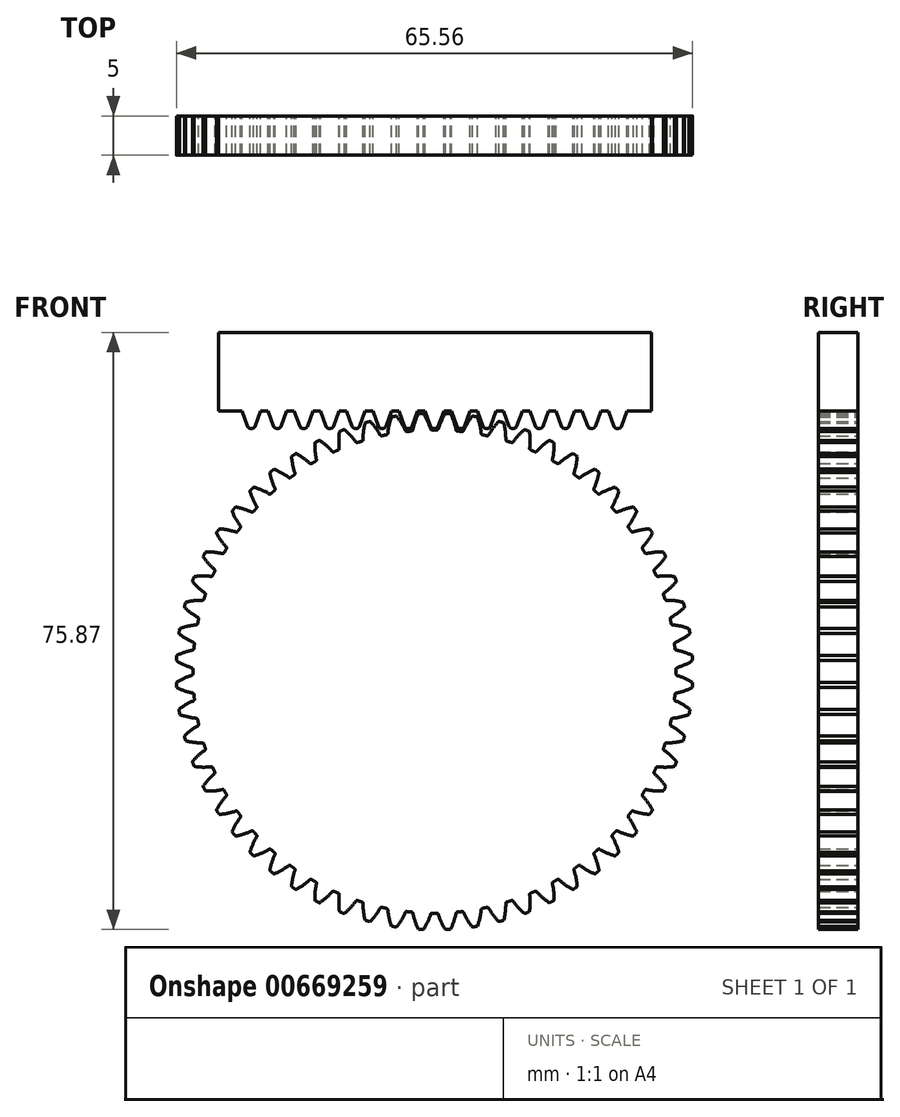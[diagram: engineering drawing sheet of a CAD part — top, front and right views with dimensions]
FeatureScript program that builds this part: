
annotation { "Feature Type Name" : "Feature", "Feature Type Description" : "" }
export const myFeature = defineFeature(function(context is Context, id is Id, definition is map)
    precondition{}
    {
        {
            var Q0;
            Q0=qCreatedBy(makeId("Front.planeOp"),FACE);
            var sketch = newSketch(context, id + "F0", { "sketchPlane" : qUnion([Q0])});
            skCircle(sketch, "E0", {"center": v(0, 0) * mm, "radius": 31.75 * mm, "construction": true});
            skCircle(sketch, "E1", {"center": v(0, 0) * mm, "radius": 30.7 * mm, "construction": true});
            skCircle(sketch, "E2", {"center": v(0, 0) * mm, "radius": 32.81 * mm, "construction": true});
            skCircle(sketch, "E3", {"center": v(0, 0) * mm, "radius": 29.63 * mm, "construction": true});
            skLineSegment(sketch, "E4", {"start": v(0, 0) * mm, "end": v(-1.03, 39.18) * mm, "construction": true});
            skLineSegment(sketch, "E5", {"start": v(0, 0) * mm, "end": v(-3.06, 38.83) * mm, "construction": true});
            skLineSegment(sketch, "E6", {"start": v(0, 0) * mm, "end": v(-2.1, 39.97) * mm, "construction": true});
            skLineSegment(sketch, "E7", {"start": v(-0.83, 31.74) * mm, "end": v(-20.7, 31.22) * mm, "construction": true});
            skLineSegment(sketch, "E8", {"start": v(-0.83, 31.74) * mm, "end": v(-21.46, 23.61) * mm, "construction": true});
            skCircle(sketch, "E9", {"center": v(-0.83, 31.74) * mm, "radius": 7.94 * mm, "construction": true});
            skArc(sketch, "E10", {"start": v(-0.5, 30.83) * mm, "mid": v(-0.88, 31.84) * mm, "end": v(-1.4, 32.78) * mm});
            skArc(sketch, "E11", {"start": v(-1.4, 32.78) * mm, "mid": v(-1.55, 32.77) * mm, "end": v(-1.72, 32.77) * mm});
            skArc(sketch, "E12", {"start": v(0, 30.7) * mm, "mid": v(-0.15, 30.69) * mm, "end": v(-0.3, 30.69) * mm});
            skArc(sketch, "E13.MirrorCS", {"start": v(-2.04, 32.75) * mm, "mid": v(-1.88, 32.76) * mm, "end": v(-1.72, 32.77) * mm});
            skArc(sketch, "E14.MirrorCS", {"start": v(-2.73, 30.71) * mm, "mid": v(-2.46, 31.75) * mm, "end": v(-2.04, 32.75) * mm});
            skArc(sketch, "E15.MirrorCS", {"start": v(-3.2, 30.52) * mm, "mid": v(-3.06, 30.54) * mm, "end": v(-2.91, 30.55) * mm});
            skPoint(sketch, "E16.visualSharp", {"position": v(-2.76, 30.57) * mm});
            skArc(sketch, "E16.filletArc", {"start": v(-2.91, 30.55) * mm, "mid": v(-2.8, 30.6) * mm, "end": v(-2.73, 30.71) * mm});
            skPoint(sketch, "E17.visualSharp", {"position": v(-0.45, 30.69) * mm});
            skArc(sketch, "E17.filletArc", {"start": v(-0.5, 30.83) * mm, "mid": v(-0.42, 30.73) * mm, "end": v(-0.3, 30.69) * mm});
            skArc(sketch, "E18.1.0", {"start": v(0, 30.7) * mm, "mid": v(0.15, 30.69) * mm, "end": v(0.3, 30.69) * mm});
            skArc(sketch, "E18.1.1", {"start": v(0.3, 30.69) * mm, "mid": v(0.42, 30.73) * mm, "end": v(0.5, 30.83) * mm});
            skArc(sketch, "E18.1.2", {"start": v(0.5, 30.83) * mm, "mid": v(0.88, 31.84) * mm, "end": v(1.4, 32.78) * mm});
            skArc(sketch, "E18.1.3", {"start": v(2.73, 30.71) * mm, "mid": v(2.8, 30.6) * mm, "end": v(2.91, 30.55) * mm});
            skArc(sketch, "E18.1.4", {"start": v(3.2, 30.52) * mm, "mid": v(3.06, 30.54) * mm, "end": v(2.91, 30.55) * mm});
            skArc(sketch, "E18.1.5", {"start": v(2.73, 30.71) * mm, "mid": v(2.46, 31.75) * mm, "end": v(2.04, 32.75) * mm});
            skArc(sketch, "E18.1.6", {"start": v(1.4, 32.78) * mm, "mid": v(1.55, 32.77) * mm, "end": v(1.72, 32.77) * mm});
            skArc(sketch, "E18.1.7", {"start": v(2.04, 32.75) * mm, "mid": v(1.88, 32.76) * mm, "end": v(1.72, 32.77) * mm});
            skArc(sketch, "E18.2.0", {"start": v(3.2, 30.52) * mm, "mid": v(3.36, 30.5) * mm, "end": v(3.5, 30.49) * mm});
            skArc(sketch, "E18.2.1", {"start": v(3.5, 30.49) * mm, "mid": v(3.63, 30.52) * mm, "end": v(3.71, 30.6) * mm});
            skArc(sketch, "E18.2.2", {"start": v(3.71, 30.6) * mm, "mid": v(4.2, 31.57) * mm, "end": v(4.81, 32.46) * mm});
            skArc(sketch, "E18.2.3", {"start": v(5.93, 30.26) * mm, "mid": v(5.98, 30.14) * mm, "end": v(6.09, 30.08) * mm});
            skArc(sketch, "E18.2.4", {"start": v(6.38, 30.02) * mm, "mid": v(6.24, 30.05) * mm, "end": v(6.09, 30.08) * mm});
            skArc(sketch, "E18.2.5", {"start": v(5.93, 30.26) * mm, "mid": v(5.76, 31.32) * mm, "end": v(5.45, 32.35) * mm});
            skArc(sketch, "E18.2.6", {"start": v(4.81, 32.46) * mm, "mid": v(4.97, 32.43) * mm, "end": v(5.13, 32.4) * mm});
            skArc(sketch, "E18.2.7", {"start": v(5.45, 32.35) * mm, "mid": v(5.3, 32.38) * mm, "end": v(5.13, 32.4) * mm});
            skArc(sketch, "E18.3.0", {"start": v(6.38, 30.02) * mm, "mid": v(6.53, 29.99) * mm, "end": v(6.67, 29.96) * mm});
            skArc(sketch, "E18.3.1", {"start": v(6.67, 29.96) * mm, "mid": v(6.8, 29.97) * mm, "end": v(6.89, 30.05) * mm});
            skArc(sketch, "E18.3.2", {"start": v(6.89, 30.05) * mm, "mid": v(7.47, 30.96) * mm, "end": v(8.18, 31.77) * mm});
            skArc(sketch, "E18.3.3", {"start": v(9.06, 29.47) * mm, "mid": v(9.1, 29.35) * mm, "end": v(9.2, 29.28) * mm});
            skArc(sketch, "E18.3.4", {"start": v(9.48, 29.19) * mm, "mid": v(9.34, 29.23) * mm, "end": v(9.2, 29.28) * mm});
            skArc(sketch, "E18.3.5", {"start": v(9.06, 29.47) * mm, "mid": v(9, 30.55) * mm, "end": v(8.8, 31.6) * mm});
            skArc(sketch, "E18.3.6", {"start": v(8.18, 31.77) * mm, "mid": v(8.33, 31.73) * mm, "end": v(8.5, 31.7) * mm});
            skArc(sketch, "E18.3.7", {"start": v(8.8, 31.6) * mm, "mid": v(8.65, 31.65) * mm, "end": v(8.5, 31.7) * mm});
            skArc(sketch, "E18.4.0", {"start": v(9.48, 29.19) * mm, "mid": v(9.63, 29.14) * mm, "end": v(9.77, 29.1) * mm});
            skArc(sketch, "E18.4.1", {"start": v(9.77, 29.1) * mm, "mid": v(9.9, 29.1) * mm, "end": v(10, 29.17) * mm});
            skArc(sketch, "E18.4.2", {"start": v(10, 29.17) * mm, "mid": v(10.67, 30) * mm, "end": v(11.45, 30.75) * mm});
            skArc(sketch, "E18.4.3", {"start": v(12.1, 28.36) * mm, "mid": v(12.12, 28.24) * mm, "end": v(12.21, 28.16) * mm});
            skArc(sketch, "E18.4.4", {"start": v(12.48, 28.04) * mm, "mid": v(12.35, 28.1) * mm, "end": v(12.21, 28.16) * mm});
            skArc(sketch, "E18.4.5", {"start": v(12.1, 28.36) * mm, "mid": v(12.15, 29.44) * mm, "end": v(12.06, 30.51) * mm});
            skArc(sketch, "E18.4.6", {"start": v(11.45, 30.75) * mm, "mid": v(11.6, 30.69) * mm, "end": v(11.76, 30.63) * mm});
            skArc(sketch, "E18.4.7", {"start": v(12.06, 30.51) * mm, "mid": v(11.9, 30.57) * mm, "end": v(11.76, 30.63) * mm});
            skArc(sketch, "E18.5.0", {"start": v(12.48, 28.04) * mm, "mid": v(12.62, 27.98) * mm, "end": v(12.75, 27.91) * mm});
            skArc(sketch, "E18.5.1", {"start": v(12.75, 27.91) * mm, "mid": v(12.88, 27.9) * mm, "end": v(12.99, 27.97) * mm});
            skArc(sketch, "E18.5.2", {"start": v(12.99, 27.97) * mm, "mid": v(13.75, 28.73) * mm, "end": v(14.6, 29.38) * mm});
            skArc(sketch, "E18.5.3", {"start": v(15, 26.94) * mm, "mid": v(15, 26.82) * mm, "end": v(15.09, 26.73) * mm});
            skArc(sketch, "E18.5.4", {"start": v(15.35, 26.58) * mm, "mid": v(15.22, 26.65) * mm, "end": v(15.09, 26.73) * mm});
            skArc(sketch, "E18.5.5", {"start": v(15, 26.94) * mm, "mid": v(15.16, 28) * mm, "end": v(15.18, 29.08) * mm});
            skArc(sketch, "E18.5.6", {"start": v(14.6, 29.38) * mm, "mid": v(14.75, 29.3) * mm, "end": v(14.9, 29.23) * mm});
            skArc(sketch, "E18.5.7", {"start": v(15.18, 29.08) * mm, "mid": v(15.04, 29.16) * mm, "end": v(14.9, 29.23) * mm});
            skArc(sketch, "E18.6.0", {"start": v(15.34, 26.58) * mm, "mid": v(15.47, 26.5) * mm, "end": v(15.6, 26.43) * mm});
            skArc(sketch, "E18.6.1", {"start": v(15.6, 26.43) * mm, "mid": v(15.73, 26.4) * mm, "end": v(15.84, 26.45) * mm});
            skArc(sketch, "E18.6.2", {"start": v(15.84, 26.45) * mm, "mid": v(16.68, 27.13) * mm, "end": v(17.6, 27.7) * mm});
            skArc(sketch, "E18.6.3", {"start": v(17.72, 25.23) * mm, "mid": v(17.72, 25.1) * mm, "end": v(17.8, 25) * mm});
            skArc(sketch, "E18.6.4", {"start": v(18.04, 24.83) * mm, "mid": v(17.92, 24.92) * mm, "end": v(17.8, 25) * mm});
            skArc(sketch, "E18.6.5", {"start": v(17.72, 25.23) * mm, "mid": v(18, 26.27) * mm, "end": v(18.14, 27.34) * mm});
            skArc(sketch, "E18.6.6", {"start": v(17.6, 27.7) * mm, "mid": v(17.73, 27.6) * mm, "end": v(17.87, 27.52) * mm});
            skArc(sketch, "E18.6.7", {"start": v(18.14, 27.34) * mm, "mid": v(18, 27.43) * mm, "end": v(17.87, 27.52) * mm});
            skArc(sketch, "E18.7.0", {"start": v(18.04, 24.83) * mm, "mid": v(18.16, 24.74) * mm, "end": v(18.28, 24.65) * mm});
            skArc(sketch, "E18.7.1", {"start": v(18.28, 24.65) * mm, "mid": v(18.4, 24.61) * mm, "end": v(18.52, 24.65) * mm});
            skArc(sketch, "E18.7.2", {"start": v(18.52, 24.65) * mm, "mid": v(19.42, 25.24) * mm, "end": v(20.4, 25.7) * mm});
            skArc(sketch, "E18.7.3", {"start": v(20.26, 23.24) * mm, "mid": v(20.25, 23.11) * mm, "end": v(20.31, 23) * mm});
            skArc(sketch, "E18.7.4", {"start": v(20.54, 22.8) * mm, "mid": v(20.42, 22.9) * mm, "end": v(20.31, 23) * mm});
            skArc(sketch, "E18.7.5", {"start": v(20.26, 23.24) * mm, "mid": v(20.65, 24.24) * mm, "end": v(20.9, 25.3) * mm});
            skArc(sketch, "E18.7.6", {"start": v(20.4, 25.7) * mm, "mid": v(20.52, 25.6) * mm, "end": v(20.65, 25.5) * mm});
            skArc(sketch, "E18.7.7", {"start": v(20.9, 25.3) * mm, "mid": v(20.77, 25.4) * mm, "end": v(20.65, 25.5) * mm});
            skArc(sketch, "E18.8.0", {"start": v(20.54, 22.8) * mm, "mid": v(20.65, 22.7) * mm, "end": v(20.76, 22.6) * mm});
            skArc(sketch, "E18.8.1", {"start": v(20.76, 22.6) * mm, "mid": v(20.87, 22.56) * mm, "end": v(21, 22.58) * mm});
            skArc(sketch, "E18.8.2", {"start": v(21, 22.58) * mm, "mid": v(21.95, 23.07) * mm, "end": v(22.97, 23.43) * mm});
            skArc(sketch, "E18.8.3", {"start": v(22.58, 21) * mm, "mid": v(22.56, 20.87) * mm, "end": v(22.6, 20.76) * mm});
            skArc(sketch, "E18.8.4", {"start": v(22.8, 20.54) * mm, "mid": v(22.7, 20.65) * mm, "end": v(22.6, 20.76) * mm});
            skArc(sketch, "E18.8.5", {"start": v(22.58, 21) * mm, "mid": v(23.07, 21.95) * mm, "end": v(23.43, 22.97) * mm});
            skArc(sketch, "E18.8.6", {"start": v(22.97, 23.43) * mm, "mid": v(23.08, 23.31) * mm, "end": v(23.2, 23.2) * mm});
            skArc(sketch, "E18.8.7", {"start": v(23.43, 22.97) * mm, "mid": v(23.31, 23.08) * mm, "end": v(23.2, 23.2) * mm});
            skArc(sketch, "E18.9.0", {"start": v(22.8, 20.54) * mm, "mid": v(22.9, 20.42) * mm, "end": v(23, 20.31) * mm});
            skArc(sketch, "E18.9.1", {"start": v(23, 20.31) * mm, "mid": v(23.11, 20.25) * mm, "end": v(23.24, 20.26) * mm});
            skArc(sketch, "E18.9.2", {"start": v(23.24, 20.26) * mm, "mid": v(24.24, 20.65) * mm, "end": v(25.3, 20.9) * mm});
            skArc(sketch, "E18.9.3", {"start": v(24.65, 18.52) * mm, "mid": v(24.61, 18.4) * mm, "end": v(24.65, 18.28) * mm});
            skArc(sketch, "E18.9.4", {"start": v(24.83, 18.04) * mm, "mid": v(24.74, 18.16) * mm, "end": v(24.65, 18.28) * mm});
            skArc(sketch, "E18.9.5", {"start": v(24.65, 18.52) * mm, "mid": v(25.24, 19.42) * mm, "end": v(25.7, 20.4) * mm});
            skArc(sketch, "E18.9.6", {"start": v(25.3, 20.9) * mm, "mid": v(25.4, 20.77) * mm, "end": v(25.5, 20.65) * mm});
            skArc(sketch, "E18.9.7", {"start": v(25.7, 20.4) * mm, "mid": v(25.6, 20.52) * mm, "end": v(25.5, 20.65) * mm});
            skArc(sketch, "E18.10.0", {"start": v(24.83, 18.04) * mm, "mid": v(24.92, 17.92) * mm, "end": v(25, 17.8) * mm});
            skArc(sketch, "E18.10.1", {"start": v(25, 17.8) * mm, "mid": v(25.1, 17.72) * mm, "end": v(25.23, 17.72) * mm});
            skArc(sketch, "E18.10.2", {"start": v(25.23, 17.72) * mm, "mid": v(26.27, 18) * mm, "end": v(27.34, 18.14) * mm});
            skArc(sketch, "E18.10.3", {"start": v(26.45, 15.84) * mm, "mid": v(26.4, 15.73) * mm, "end": v(26.43, 15.6) * mm});
            skArc(sketch, "E18.10.4", {"start": v(26.58, 15.35) * mm, "mid": v(26.5, 15.47) * mm, "end": v(26.43, 15.6) * mm});
            skArc(sketch, "E18.10.5", {"start": v(26.45, 15.84) * mm, "mid": v(27.13, 16.68) * mm, "end": v(27.7, 17.6) * mm});
            skArc(sketch, "E18.10.6", {"start": v(27.34, 18.14) * mm, "mid": v(27.43, 18) * mm, "end": v(27.52, 17.87) * mm});
            skArc(sketch, "E18.10.7", {"start": v(27.7, 17.6) * mm, "mid": v(27.6, 17.73) * mm, "end": v(27.52, 17.87) * mm});
            skArc(sketch, "E18.11.0", {"start": v(26.58, 15.35) * mm, "mid": v(26.65, 15.22) * mm, "end": v(26.73, 15.09) * mm});
            skArc(sketch, "E18.11.1", {"start": v(26.73, 15.09) * mm, "mid": v(26.82, 15) * mm, "end": v(26.94, 15) * mm});
            skArc(sketch, "E18.11.2", {"start": v(26.94, 15) * mm, "mid": v(28, 15.16) * mm, "end": v(29.08, 15.18) * mm});
            skArc(sketch, "E18.11.3", {"start": v(27.97, 12.99) * mm, "mid": v(27.9, 12.88) * mm, "end": v(27.91, 12.75) * mm});
            skArc(sketch, "E18.11.4", {"start": v(28.04, 12.48) * mm, "mid": v(27.98, 12.62) * mm, "end": v(27.91, 12.75) * mm});
            skArc(sketch, "E18.11.5", {"start": v(27.97, 12.99) * mm, "mid": v(28.73, 13.75) * mm, "end": v(29.38, 14.6) * mm});
            skArc(sketch, "E18.11.6", {"start": v(29.08, 15.18) * mm, "mid": v(29.16, 15.04) * mm, "end": v(29.23, 14.9) * mm});
            skArc(sketch, "E18.11.7", {"start": v(29.38, 14.6) * mm, "mid": v(29.3, 14.75) * mm, "end": v(29.23, 14.9) * mm});
            skArc(sketch, "E18.12.0", {"start": v(28.04, 12.48) * mm, "mid": v(28.1, 12.35) * mm, "end": v(28.16, 12.21) * mm});
            skArc(sketch, "E18.12.1", {"start": v(28.16, 12.21) * mm, "mid": v(28.24, 12.12) * mm, "end": v(28.36, 12.1) * mm});
            skArc(sketch, "E18.12.2", {"start": v(28.36, 12.1) * mm, "mid": v(29.44, 12.15) * mm, "end": v(30.51, 12.06) * mm});
            skArc(sketch, "E18.12.3", {"start": v(29.17, 10) * mm, "mid": v(29.1, 9.9) * mm, "end": v(29.1, 9.77) * mm});
            skArc(sketch, "E18.12.4", {"start": v(29.19, 9.48) * mm, "mid": v(29.14, 9.63) * mm, "end": v(29.1, 9.77) * mm});
            skArc(sketch, "E18.12.5", {"start": v(29.17, 10) * mm, "mid": v(30, 10.67) * mm, "end": v(30.75, 11.45) * mm});
            skArc(sketch, "E18.12.6", {"start": v(30.51, 12.06) * mm, "mid": v(30.57, 11.9) * mm, "end": v(30.63, 11.76) * mm});
            skArc(sketch, "E18.12.7", {"start": v(30.75, 11.45) * mm, "mid": v(30.69, 11.6) * mm, "end": v(30.63, 11.76) * mm});
            skArc(sketch, "E18.13.0", {"start": v(29.19, 9.48) * mm, "mid": v(29.23, 9.34) * mm, "end": v(29.28, 9.2) * mm});
            skArc(sketch, "E18.13.1", {"start": v(29.28, 9.2) * mm, "mid": v(29.35, 9.1) * mm, "end": v(29.47, 9.06) * mm});
            skArc(sketch, "E18.13.2", {"start": v(29.47, 9.06) * mm, "mid": v(30.55, 9) * mm, "end": v(31.6, 8.8) * mm});
            skArc(sketch, "E18.13.3", {"start": v(30.05, 6.89) * mm, "mid": v(29.97, 6.8) * mm, "end": v(29.96, 6.67) * mm});
            skArc(sketch, "E18.13.4", {"start": v(30.02, 6.38) * mm, "mid": v(29.99, 6.53) * mm, "end": v(29.96, 6.67) * mm});
            skArc(sketch, "E18.13.5", {"start": v(30.05, 6.89) * mm, "mid": v(30.96, 7.47) * mm, "end": v(31.77, 8.18) * mm});
            skArc(sketch, "E18.13.6", {"start": v(31.6, 8.8) * mm, "mid": v(31.65, 8.65) * mm, "end": v(31.7, 8.5) * mm});
            skArc(sketch, "E18.13.7", {"start": v(31.77, 8.18) * mm, "mid": v(31.73, 8.33) * mm, "end": v(31.7, 8.5) * mm});
            skArc(sketch, "E18.14.0", {"start": v(30.02, 6.38) * mm, "mid": v(30.05, 6.24) * mm, "end": v(30.08, 6.09) * mm});
            skArc(sketch, "E18.14.1", {"start": v(30.08, 6.09) * mm, "mid": v(30.14, 5.98) * mm, "end": v(30.26, 5.93) * mm});
            skArc(sketch, "E18.14.2", {"start": v(30.26, 5.93) * mm, "mid": v(31.32, 5.76) * mm, "end": v(32.35, 5.45) * mm});
            skArc(sketch, "E18.14.3", {"start": v(30.6, 3.71) * mm, "mid": v(30.52, 3.63) * mm, "end": v(30.49, 3.5) * mm});
            skArc(sketch, "E18.14.4", {"start": v(30.52, 3.2) * mm, "mid": v(30.5, 3.36) * mm, "end": v(30.49, 3.5) * mm});
            skArc(sketch, "E18.14.5", {"start": v(30.6, 3.71) * mm, "mid": v(31.57, 4.2) * mm, "end": v(32.46, 4.81) * mm});
            skArc(sketch, "E18.14.6", {"start": v(32.35, 5.45) * mm, "mid": v(32.38, 5.3) * mm, "end": v(32.4, 5.13) * mm});
            skArc(sketch, "E18.14.7", {"start": v(32.46, 4.81) * mm, "mid": v(32.43, 4.97) * mm, "end": v(32.4, 5.13) * mm});
            skArc(sketch, "E18.15.0", {"start": v(30.52, 3.2) * mm, "mid": v(30.54, 3.06) * mm, "end": v(30.55, 2.91) * mm});
            skArc(sketch, "E18.15.1", {"start": v(30.55, 2.91) * mm, "mid": v(30.6, 2.8) * mm, "end": v(30.71, 2.73) * mm});
            skArc(sketch, "E18.15.2", {"start": v(30.71, 2.73) * mm, "mid": v(31.75, 2.46) * mm, "end": v(32.75, 2.04) * mm});
            skArc(sketch, "E18.15.3", {"start": v(30.83, 0.5) * mm, "mid": v(30.73, 0.42) * mm, "end": v(30.69, 0.3) * mm});
            skArc(sketch, "E18.15.4", {"start": v(30.7, 0) * mm, "mid": v(30.69, 0.15) * mm, "end": v(30.69, 0.3) * mm});
            skArc(sketch, "E18.15.5", {"start": v(30.83, 0.5) * mm, "mid": v(31.84, 0.88) * mm, "end": v(32.78, 1.4) * mm});
            skArc(sketch, "E18.15.6", {"start": v(32.75, 2.04) * mm, "mid": v(32.76, 1.88) * mm, "end": v(32.77, 1.72) * mm});
            skArc(sketch, "E18.15.7", {"start": v(32.78, 1.4) * mm, "mid": v(32.77, 1.55) * mm, "end": v(32.77, 1.72) * mm});
            skArc(sketch, "E18.16.0", {"start": v(30.7, 0) * mm, "mid": v(30.69, -0.15) * mm, "end": v(30.69, -0.3) * mm});
            skArc(sketch, "E18.16.1", {"start": v(30.69, -0.3) * mm, "mid": v(30.73, -0.42) * mm, "end": v(30.83, -0.5) * mm});
            skArc(sketch, "E18.16.2", {"start": v(30.83, -0.5) * mm, "mid": v(31.84, -0.88) * mm, "end": v(32.78, -1.4) * mm});
            skArc(sketch, "E18.16.3", {"start": v(30.71, -2.73) * mm, "mid": v(30.6, -2.8) * mm, "end": v(30.55, -2.91) * mm});
            skArc(sketch, "E18.16.4", {"start": v(30.52, -3.2) * mm, "mid": v(30.54, -3.06) * mm, "end": v(30.55, -2.91) * mm});
            skArc(sketch, "E18.16.5", {"start": v(30.71, -2.73) * mm, "mid": v(31.75, -2.46) * mm, "end": v(32.75, -2.04) * mm});
            skArc(sketch, "E18.16.6", {"start": v(32.78, -1.4) * mm, "mid": v(32.77, -1.55) * mm, "end": v(32.77, -1.72) * mm});
            skArc(sketch, "E18.16.7", {"start": v(32.75, -2.04) * mm, "mid": v(32.76, -1.88) * mm, "end": v(32.77, -1.72) * mm});
            skArc(sketch, "E18.17.0", {"start": v(30.52, -3.2) * mm, "mid": v(30.5, -3.36) * mm, "end": v(30.49, -3.5) * mm});
            skArc(sketch, "E18.17.1", {"start": v(30.49, -3.5) * mm, "mid": v(30.52, -3.63) * mm, "end": v(30.6, -3.71) * mm});
            skArc(sketch, "E18.17.2", {"start": v(30.6, -3.71) * mm, "mid": v(31.57, -4.2) * mm, "end": v(32.46, -4.81) * mm});
            skArc(sketch, "E18.17.3", {"start": v(30.26, -5.93) * mm, "mid": v(30.14, -5.98) * mm, "end": v(30.08, -6.09) * mm});
            skArc(sketch, "E18.17.4", {"start": v(30.02, -6.38) * mm, "mid": v(30.05, -6.24) * mm, "end": v(30.08, -6.09) * mm});
            skArc(sketch, "E18.17.5", {"start": v(30.26, -5.93) * mm, "mid": v(31.32, -5.76) * mm, "end": v(32.35, -5.45) * mm});
            skArc(sketch, "E18.17.6", {"start": v(32.46, -4.81) * mm, "mid": v(32.43, -4.97) * mm, "end": v(32.4, -5.13) * mm});
            skArc(sketch, "E18.17.7", {"start": v(32.35, -5.45) * mm, "mid": v(32.38, -5.3) * mm, "end": v(32.4, -5.13) * mm});
            skArc(sketch, "E18.18.0", {"start": v(30.02, -6.38) * mm, "mid": v(29.99, -6.53) * mm, "end": v(29.96, -6.67) * mm});
            skArc(sketch, "E18.18.1", {"start": v(29.96, -6.67) * mm, "mid": v(29.97, -6.8) * mm, "end": v(30.05, -6.89) * mm});
            skArc(sketch, "E18.18.2", {"start": v(30.05, -6.89) * mm, "mid": v(30.96, -7.47) * mm, "end": v(31.77, -8.18) * mm});
            skArc(sketch, "E18.18.3", {"start": v(29.47, -9.06) * mm, "mid": v(29.35, -9.1) * mm, "end": v(29.28, -9.2) * mm});
            skArc(sketch, "E18.18.4", {"start": v(29.19, -9.48) * mm, "mid": v(29.23, -9.34) * mm, "end": v(29.28, -9.2) * mm});
            skArc(sketch, "E18.18.5", {"start": v(29.47, -9.06) * mm, "mid": v(30.55, -9) * mm, "end": v(31.6, -8.8) * mm});
            skArc(sketch, "E18.18.6", {"start": v(31.77, -8.18) * mm, "mid": v(31.73, -8.33) * mm, "end": v(31.7, -8.5) * mm});
            skArc(sketch, "E18.18.7", {"start": v(31.6, -8.8) * mm, "mid": v(31.65, -8.65) * mm, "end": v(31.7, -8.5) * mm});
            skArc(sketch, "E18.19.0", {"start": v(29.19, -9.48) * mm, "mid": v(29.14, -9.63) * mm, "end": v(29.1, -9.77) * mm});
            skArc(sketch, "E18.19.1", {"start": v(29.1, -9.77) * mm, "mid": v(29.1, -9.9) * mm, "end": v(29.17, -10) * mm});
            skArc(sketch, "E18.19.2", {"start": v(29.17, -10) * mm, "mid": v(30, -10.67) * mm, "end": v(30.75, -11.45) * mm});
            skArc(sketch, "E18.19.3", {"start": v(28.36, -12.1) * mm, "mid": v(28.24, -12.12) * mm, "end": v(28.16, -12.21) * mm});
            skArc(sketch, "E18.19.4", {"start": v(28.04, -12.48) * mm, "mid": v(28.1, -12.35) * mm, "end": v(28.16, -12.21) * mm});
            skArc(sketch, "E18.19.5", {"start": v(28.36, -12.1) * mm, "mid": v(29.44, -12.15) * mm, "end": v(30.51, -12.06) * mm});
            skArc(sketch, "E18.19.6", {"start": v(30.75, -11.45) * mm, "mid": v(30.69, -11.6) * mm, "end": v(30.63, -11.76) * mm});
            skArc(sketch, "E18.19.7", {"start": v(30.51, -12.06) * mm, "mid": v(30.57, -11.9) * mm, "end": v(30.63, -11.76) * mm});
            skArc(sketch, "E18.20.0", {"start": v(28.04, -12.48) * mm, "mid": v(27.98, -12.62) * mm, "end": v(27.91, -12.75) * mm});
            skArc(sketch, "E18.20.1", {"start": v(27.91, -12.75) * mm, "mid": v(27.9, -12.88) * mm, "end": v(27.97, -12.99) * mm});
            skArc(sketch, "E18.20.2", {"start": v(27.97, -12.99) * mm, "mid": v(28.73, -13.75) * mm, "end": v(29.38, -14.6) * mm});
            skArc(sketch, "E18.20.3", {"start": v(26.94, -15) * mm, "mid": v(26.82, -15) * mm, "end": v(26.73, -15.09) * mm});
            skArc(sketch, "E18.20.4", {"start": v(26.58, -15.34) * mm, "mid": v(26.65, -15.22) * mm, "end": v(26.73, -15.09) * mm});
            skArc(sketch, "E18.20.5", {"start": v(26.94, -15) * mm, "mid": v(28, -15.16) * mm, "end": v(29.08, -15.18) * mm});
            skArc(sketch, "E18.20.6", {"start": v(29.38, -14.6) * mm, "mid": v(29.3, -14.75) * mm, "end": v(29.23, -14.9) * mm});
            skArc(sketch, "E18.20.7", {"start": v(29.08, -15.18) * mm, "mid": v(29.16, -15.04) * mm, "end": v(29.23, -14.9) * mm});
            skArc(sketch, "E18.21.0", {"start": v(26.58, -15.34) * mm, "mid": v(26.5, -15.47) * mm, "end": v(26.43, -15.6) * mm});
            skArc(sketch, "E18.21.1", {"start": v(26.43, -15.6) * mm, "mid": v(26.4, -15.73) * mm, "end": v(26.45, -15.84) * mm});
            skArc(sketch, "E18.21.2", {"start": v(26.45, -15.84) * mm, "mid": v(27.13, -16.68) * mm, "end": v(27.7, -17.6) * mm});
            skArc(sketch, "E18.21.3", {"start": v(25.23, -17.72) * mm, "mid": v(25.1, -17.72) * mm, "end": v(25, -17.8) * mm});
            skArc(sketch, "E18.21.4", {"start": v(24.83, -18.04) * mm, "mid": v(24.92, -17.92) * mm, "end": v(25, -17.8) * mm});
            skArc(sketch, "E18.21.5", {"start": v(25.23, -17.72) * mm, "mid": v(26.27, -18) * mm, "end": v(27.34, -18.14) * mm});
            skArc(sketch, "E18.21.6", {"start": v(27.7, -17.6) * mm, "mid": v(27.6, -17.73) * mm, "end": v(27.52, -17.87) * mm});
            skArc(sketch, "E18.21.7", {"start": v(27.34, -18.14) * mm, "mid": v(27.43, -18) * mm, "end": v(27.52, -17.87) * mm});
            skArc(sketch, "E18.22.0", {"start": v(24.83, -18.04) * mm, "mid": v(24.74, -18.16) * mm, "end": v(24.65, -18.28) * mm});
            skArc(sketch, "E18.22.1", {"start": v(24.65, -18.28) * mm, "mid": v(24.61, -18.4) * mm, "end": v(24.65, -18.52) * mm});
            skArc(sketch, "E18.22.2", {"start": v(24.65, -18.52) * mm, "mid": v(25.24, -19.42) * mm, "end": v(25.7, -20.4) * mm});
            skArc(sketch, "E18.22.3", {"start": v(23.24, -20.26) * mm, "mid": v(23.11, -20.25) * mm, "end": v(23, -20.31) * mm});
            skArc(sketch, "E18.22.4", {"start": v(22.8, -20.54) * mm, "mid": v(22.9, -20.42) * mm, "end": v(23, -20.31) * mm});
            skArc(sketch, "E18.22.5", {"start": v(23.24, -20.26) * mm, "mid": v(24.24, -20.65) * mm, "end": v(25.3, -20.9) * mm});
            skArc(sketch, "E18.22.6", {"start": v(25.7, -20.4) * mm, "mid": v(25.6, -20.52) * mm, "end": v(25.5, -20.65) * mm});
            skArc(sketch, "E18.22.7", {"start": v(25.3, -20.9) * mm, "mid": v(25.4, -20.77) * mm, "end": v(25.5, -20.65) * mm});
            skArc(sketch, "E18.23.0", {"start": v(22.8, -20.54) * mm, "mid": v(22.7, -20.65) * mm, "end": v(22.6, -20.76) * mm});
            skArc(sketch, "E18.23.1", {"start": v(22.6, -20.76) * mm, "mid": v(22.56, -20.87) * mm, "end": v(22.58, -21) * mm});
            skArc(sketch, "E18.23.2", {"start": v(22.58, -21) * mm, "mid": v(23.07, -21.95) * mm, "end": v(23.43, -22.97) * mm});
            skArc(sketch, "E18.23.3", {"start": v(21, -22.58) * mm, "mid": v(20.87, -22.56) * mm, "end": v(20.76, -22.6) * mm});
            skArc(sketch, "E18.23.4", {"start": v(20.54, -22.8) * mm, "mid": v(20.65, -22.7) * mm, "end": v(20.76, -22.6) * mm});
            skArc(sketch, "E18.23.5", {"start": v(21, -22.58) * mm, "mid": v(21.95, -23.07) * mm, "end": v(22.97, -23.43) * mm});
            skArc(sketch, "E18.23.6", {"start": v(23.43, -22.97) * mm, "mid": v(23.31, -23.08) * mm, "end": v(23.2, -23.2) * mm});
            skArc(sketch, "E18.23.7", {"start": v(22.97, -23.43) * mm, "mid": v(23.08, -23.31) * mm, "end": v(23.2, -23.2) * mm});
            skArc(sketch, "E18.24.0", {"start": v(20.54, -22.8) * mm, "mid": v(20.42, -22.9) * mm, "end": v(20.31, -23) * mm});
            skArc(sketch, "E18.24.1", {"start": v(20.31, -23) * mm, "mid": v(20.25, -23.11) * mm, "end": v(20.26, -23.24) * mm});
            skArc(sketch, "E18.24.2", {"start": v(20.26, -23.24) * mm, "mid": v(20.65, -24.24) * mm, "end": v(20.9, -25.3) * mm});
            skArc(sketch, "E18.24.3", {"start": v(18.52, -24.65) * mm, "mid": v(18.4, -24.61) * mm, "end": v(18.28, -24.65) * mm});
            skArc(sketch, "E18.24.4", {"start": v(18.04, -24.83) * mm, "mid": v(18.16, -24.74) * mm, "end": v(18.28, -24.65) * mm});
            skArc(sketch, "E18.24.5", {"start": v(18.52, -24.65) * mm, "mid": v(19.42, -25.24) * mm, "end": v(20.4, -25.7) * mm});
            skArc(sketch, "E18.24.6", {"start": v(20.9, -25.3) * mm, "mid": v(20.77, -25.4) * mm, "end": v(20.65, -25.5) * mm});
            skArc(sketch, "E18.24.7", {"start": v(20.4, -25.7) * mm, "mid": v(20.52, -25.6) * mm, "end": v(20.65, -25.5) * mm});
            skArc(sketch, "E18.25.0", {"start": v(18.04, -24.83) * mm, "mid": v(17.92, -24.92) * mm, "end": v(17.8, -25) * mm});
            skArc(sketch, "E18.25.1", {"start": v(17.8, -25) * mm, "mid": v(17.72, -25.1) * mm, "end": v(17.72, -25.23) * mm});
            skArc(sketch, "E18.25.2", {"start": v(17.72, -25.23) * mm, "mid": v(18, -26.27) * mm, "end": v(18.14, -27.34) * mm});
            skArc(sketch, "E18.25.3", {"start": v(15.84, -26.45) * mm, "mid": v(15.73, -26.4) * mm, "end": v(15.6, -26.43) * mm});
            skArc(sketch, "E18.25.4", {"start": v(15.35, -26.58) * mm, "mid": v(15.47, -26.5) * mm, "end": v(15.6, -26.43) * mm});
            skArc(sketch, "E18.25.5", {"start": v(15.84, -26.45) * mm, "mid": v(16.68, -27.13) * mm, "end": v(17.6, -27.7) * mm});
            skArc(sketch, "E18.25.6", {"start": v(18.14, -27.34) * mm, "mid": v(18, -27.43) * mm, "end": v(17.87, -27.52) * mm});
            skArc(sketch, "E18.25.7", {"start": v(17.6, -27.7) * mm, "mid": v(17.73, -27.6) * mm, "end": v(17.87, -27.52) * mm});
            skArc(sketch, "E18.26.0", {"start": v(15.35, -26.58) * mm, "mid": v(15.22, -26.65) * mm, "end": v(15.09, -26.73) * mm});
            skArc(sketch, "E18.26.1", {"start": v(15.09, -26.73) * mm, "mid": v(15, -26.82) * mm, "end": v(15, -26.94) * mm});
            skArc(sketch, "E18.26.2", {"start": v(15, -26.94) * mm, "mid": v(15.16, -28) * mm, "end": v(15.18, -29.08) * mm});
            skArc(sketch, "E18.26.3", {"start": v(12.99, -27.97) * mm, "mid": v(12.88, -27.9) * mm, "end": v(12.75, -27.91) * mm});
            skArc(sketch, "E18.26.4", {"start": v(12.48, -28.04) * mm, "mid": v(12.62, -27.98) * mm, "end": v(12.75, -27.91) * mm});
            skArc(sketch, "E18.26.5", {"start": v(12.99, -27.97) * mm, "mid": v(13.75, -28.73) * mm, "end": v(14.6, -29.38) * mm});
            skArc(sketch, "E18.26.6", {"start": v(15.18, -29.08) * mm, "mid": v(15.04, -29.16) * mm, "end": v(14.9, -29.23) * mm});
            skArc(sketch, "E18.26.7", {"start": v(14.6, -29.38) * mm, "mid": v(14.75, -29.3) * mm, "end": v(14.9, -29.23) * mm});
            skArc(sketch, "E18.27.0", {"start": v(12.48, -28.04) * mm, "mid": v(12.35, -28.1) * mm, "end": v(12.21, -28.16) * mm});
            skArc(sketch, "E18.27.1", {"start": v(12.21, -28.16) * mm, "mid": v(12.12, -28.24) * mm, "end": v(12.1, -28.36) * mm});
            skArc(sketch, "E18.27.2", {"start": v(12.1, -28.36) * mm, "mid": v(12.15, -29.44) * mm, "end": v(12.06, -30.51) * mm});
            skArc(sketch, "E18.27.3", {"start": v(10, -29.17) * mm, "mid": v(9.9, -29.1) * mm, "end": v(9.77, -29.1) * mm});
            skArc(sketch, "E18.27.4", {"start": v(9.48, -29.19) * mm, "mid": v(9.63, -29.14) * mm, "end": v(9.77, -29.1) * mm});
            skArc(sketch, "E18.27.5", {"start": v(10, -29.17) * mm, "mid": v(10.67, -30) * mm, "end": v(11.45, -30.75) * mm});
            skArc(sketch, "E18.27.6", {"start": v(12.06, -30.51) * mm, "mid": v(11.9, -30.57) * mm, "end": v(11.76, -30.63) * mm});
            skArc(sketch, "E18.27.7", {"start": v(11.45, -30.75) * mm, "mid": v(11.6, -30.69) * mm, "end": v(11.76, -30.63) * mm});
            skArc(sketch, "E18.28.0", {"start": v(9.48, -29.19) * mm, "mid": v(9.34, -29.23) * mm, "end": v(9.2, -29.28) * mm});
            skArc(sketch, "E18.28.1", {"start": v(9.2, -29.28) * mm, "mid": v(9.1, -29.35) * mm, "end": v(9.06, -29.47) * mm});
            skArc(sketch, "E18.28.2", {"start": v(9.06, -29.47) * mm, "mid": v(9, -30.55) * mm, "end": v(8.8, -31.6) * mm});
            skArc(sketch, "E18.28.3", {"start": v(6.89, -30.05) * mm, "mid": v(6.8, -29.97) * mm, "end": v(6.67, -29.96) * mm});
            skArc(sketch, "E18.28.4", {"start": v(6.38, -30.02) * mm, "mid": v(6.53, -29.99) * mm, "end": v(6.67, -29.96) * mm});
            skArc(sketch, "E18.28.5", {"start": v(6.89, -30.05) * mm, "mid": v(7.47, -30.96) * mm, "end": v(8.18, -31.77) * mm});
            skArc(sketch, "E18.28.6", {"start": v(8.8, -31.6) * mm, "mid": v(8.65, -31.65) * mm, "end": v(8.5, -31.7) * mm});
            skArc(sketch, "E18.28.7", {"start": v(8.18, -31.77) * mm, "mid": v(8.33, -31.73) * mm, "end": v(8.5, -31.7) * mm});
            skArc(sketch, "E18.29.0", {"start": v(6.38, -30.02) * mm, "mid": v(6.24, -30.05) * mm, "end": v(6.09, -30.08) * mm});
            skArc(sketch, "E18.29.1", {"start": v(6.09, -30.08) * mm, "mid": v(5.98, -30.14) * mm, "end": v(5.93, -30.26) * mm});
            skArc(sketch, "E18.29.2", {"start": v(5.93, -30.26) * mm, "mid": v(5.76, -31.32) * mm, "end": v(5.45, -32.35) * mm});
            skArc(sketch, "E18.29.3", {"start": v(3.71, -30.6) * mm, "mid": v(3.63, -30.52) * mm, "end": v(3.5, -30.49) * mm});
            skArc(sketch, "E18.29.4", {"start": v(3.2, -30.52) * mm, "mid": v(3.36, -30.5) * mm, "end": v(3.5, -30.49) * mm});
            skArc(sketch, "E18.29.5", {"start": v(3.71, -30.6) * mm, "mid": v(4.2, -31.57) * mm, "end": v(4.81, -32.46) * mm});
            skArc(sketch, "E18.29.6", {"start": v(5.45, -32.35) * mm, "mid": v(5.3, -32.38) * mm, "end": v(5.13, -32.4) * mm});
            skArc(sketch, "E18.29.7", {"start": v(4.81, -32.46) * mm, "mid": v(4.97, -32.43) * mm, "end": v(5.13, -32.4) * mm});
            skArc(sketch, "E18.30.0", {"start": v(3.2, -30.52) * mm, "mid": v(3.06, -30.54) * mm, "end": v(2.91, -30.55) * mm});
            skArc(sketch, "E18.30.1", {"start": v(2.91, -30.55) * mm, "mid": v(2.8, -30.6) * mm, "end": v(2.73, -30.71) * mm});
            skArc(sketch, "E18.30.2", {"start": v(2.73, -30.71) * mm, "mid": v(2.46, -31.75) * mm, "end": v(2.04, -32.75) * mm});
            skArc(sketch, "E18.30.3", {"start": v(0.5, -30.83) * mm, "mid": v(0.42, -30.73) * mm, "end": v(0.3, -30.69) * mm});
            skArc(sketch, "E18.30.4", {"start": v(0, -30.7) * mm, "mid": v(0.15, -30.69) * mm, "end": v(0.3, -30.69) * mm});
            skArc(sketch, "E18.30.5", {"start": v(0.5, -30.83) * mm, "mid": v(0.88, -31.84) * mm, "end": v(1.4, -32.78) * mm});
            skArc(sketch, "E18.30.6", {"start": v(2.04, -32.75) * mm, "mid": v(1.88, -32.76) * mm, "end": v(1.72, -32.77) * mm});
            skArc(sketch, "E18.30.7", {"start": v(1.4, -32.78) * mm, "mid": v(1.55, -32.77) * mm, "end": v(1.72, -32.77) * mm});
            skArc(sketch, "E18.31.0", {"start": v(0, -30.7) * mm, "mid": v(-0.15, -30.69) * mm, "end": v(-0.3, -30.69) * mm});
            skArc(sketch, "E18.31.1", {"start": v(-0.3, -30.69) * mm, "mid": v(-0.42, -30.73) * mm, "end": v(-0.5, -30.83) * mm});
            skArc(sketch, "E18.31.2", {"start": v(-0.5, -30.83) * mm, "mid": v(-0.88, -31.84) * mm, "end": v(-1.4, -32.78) * mm});
            skArc(sketch, "E18.31.3", {"start": v(-2.73, -30.71) * mm, "mid": v(-2.8, -30.6) * mm, "end": v(-2.91, -30.55) * mm});
            skArc(sketch, "E18.31.4", {"start": v(-3.2, -30.52) * mm, "mid": v(-3.06, -30.54) * mm, "end": v(-2.91, -30.55) * mm});
            skArc(sketch, "E18.31.5", {"start": v(-2.73, -30.71) * mm, "mid": v(-2.46, -31.75) * mm, "end": v(-2.04, -32.75) * mm});
            skArc(sketch, "E18.31.6", {"start": v(-1.4, -32.78) * mm, "mid": v(-1.55, -32.77) * mm, "end": v(-1.72, -32.77) * mm});
            skArc(sketch, "E18.31.7", {"start": v(-2.04, -32.75) * mm, "mid": v(-1.88, -32.76) * mm, "end": v(-1.72, -32.77) * mm});
            skArc(sketch, "E18.32.0", {"start": v(-3.2, -30.52) * mm, "mid": v(-3.36, -30.5) * mm, "end": v(-3.5, -30.49) * mm});
            skArc(sketch, "E18.32.1", {"start": v(-3.5, -30.49) * mm, "mid": v(-3.63, -30.52) * mm, "end": v(-3.71, -30.6) * mm});
            skArc(sketch, "E18.32.2", {"start": v(-3.71, -30.6) * mm, "mid": v(-4.2, -31.57) * mm, "end": v(-4.81, -32.46) * mm});
            skArc(sketch, "E18.32.3", {"start": v(-5.93, -30.26) * mm, "mid": v(-5.98, -30.14) * mm, "end": v(-6.09, -30.08) * mm});
            skArc(sketch, "E18.32.4", {"start": v(-6.38, -30.02) * mm, "mid": v(-6.24, -30.05) * mm, "end": v(-6.09, -30.08) * mm});
            skArc(sketch, "E18.32.5", {"start": v(-5.93, -30.26) * mm, "mid": v(-5.76, -31.32) * mm, "end": v(-5.45, -32.35) * mm});
            skArc(sketch, "E18.32.6", {"start": v(-4.81, -32.46) * mm, "mid": v(-4.97, -32.43) * mm, "end": v(-5.13, -32.4) * mm});
            skArc(sketch, "E18.32.7", {"start": v(-5.45, -32.35) * mm, "mid": v(-5.3, -32.38) * mm, "end": v(-5.13, -32.4) * mm});
            skArc(sketch, "E18.33.0", {"start": v(-6.38, -30.02) * mm, "mid": v(-6.53, -29.99) * mm, "end": v(-6.67, -29.96) * mm});
            skArc(sketch, "E18.33.1", {"start": v(-6.67, -29.96) * mm, "mid": v(-6.8, -29.97) * mm, "end": v(-6.89, -30.05) * mm});
            skArc(sketch, "E18.33.2", {"start": v(-6.89, -30.05) * mm, "mid": v(-7.47, -30.96) * mm, "end": v(-8.18, -31.77) * mm});
            skArc(sketch, "E18.33.3", {"start": v(-9.06, -29.47) * mm, "mid": v(-9.1, -29.35) * mm, "end": v(-9.2, -29.28) * mm});
            skArc(sketch, "E18.33.4", {"start": v(-9.48, -29.19) * mm, "mid": v(-9.34, -29.23) * mm, "end": v(-9.2, -29.28) * mm});
            skArc(sketch, "E18.33.5", {"start": v(-9.06, -29.47) * mm, "mid": v(-9, -30.55) * mm, "end": v(-8.8, -31.6) * mm});
            skArc(sketch, "E18.33.6", {"start": v(-8.18, -31.77) * mm, "mid": v(-8.33, -31.73) * mm, "end": v(-8.5, -31.7) * mm});
            skArc(sketch, "E18.33.7", {"start": v(-8.8, -31.6) * mm, "mid": v(-8.65, -31.65) * mm, "end": v(-8.5, -31.7) * mm});
            skArc(sketch, "E18.34.0", {"start": v(-9.48, -29.19) * mm, "mid": v(-9.63, -29.14) * mm, "end": v(-9.77, -29.1) * mm});
            skArc(sketch, "E18.34.1", {"start": v(-9.77, -29.1) * mm, "mid": v(-9.9, -29.1) * mm, "end": v(-10, -29.17) * mm});
            skArc(sketch, "E18.34.2", {"start": v(-10, -29.17) * mm, "mid": v(-10.67, -30) * mm, "end": v(-11.45, -30.75) * mm});
            skArc(sketch, "E18.34.3", {"start": v(-12.1, -28.36) * mm, "mid": v(-12.12, -28.24) * mm, "end": v(-12.21, -28.16) * mm});
            skArc(sketch, "E18.34.4", {"start": v(-12.48, -28.04) * mm, "mid": v(-12.35, -28.1) * mm, "end": v(-12.21, -28.16) * mm});
            skArc(sketch, "E18.34.5", {"start": v(-12.1, -28.36) * mm, "mid": v(-12.15, -29.44) * mm, "end": v(-12.06, -30.51) * mm});
            skArc(sketch, "E18.34.6", {"start": v(-11.45, -30.75) * mm, "mid": v(-11.6, -30.69) * mm, "end": v(-11.76, -30.63) * mm});
            skArc(sketch, "E18.34.7", {"start": v(-12.06, -30.51) * mm, "mid": v(-11.9, -30.57) * mm, "end": v(-11.76, -30.63) * mm});
            skArc(sketch, "E18.35.0", {"start": v(-12.48, -28.04) * mm, "mid": v(-12.62, -27.98) * mm, "end": v(-12.75, -27.91) * mm});
            skArc(sketch, "E18.35.1", {"start": v(-12.75, -27.91) * mm, "mid": v(-12.88, -27.9) * mm, "end": v(-12.99, -27.97) * mm});
            skArc(sketch, "E18.35.2", {"start": v(-12.99, -27.97) * mm, "mid": v(-13.75, -28.73) * mm, "end": v(-14.6, -29.38) * mm});
            skArc(sketch, "E18.35.3", {"start": v(-15, -26.94) * mm, "mid": v(-15, -26.82) * mm, "end": v(-15.09, -26.73) * mm});
            skArc(sketch, "E18.35.4", {"start": v(-15.35, -26.58) * mm, "mid": v(-15.22, -26.65) * mm, "end": v(-15.09, -26.73) * mm});
            skArc(sketch, "E18.35.5", {"start": v(-15, -26.94) * mm, "mid": v(-15.16, -28) * mm, "end": v(-15.18, -29.08) * mm});
            skArc(sketch, "E18.35.6", {"start": v(-14.6, -29.38) * mm, "mid": v(-14.75, -29.3) * mm, "end": v(-14.9, -29.23) * mm});
            skArc(sketch, "E18.35.7", {"start": v(-15.18, -29.08) * mm, "mid": v(-15.04, -29.16) * mm, "end": v(-14.9, -29.23) * mm});
            skArc(sketch, "E18.36.0", {"start": v(-15.34, -26.58) * mm, "mid": v(-15.47, -26.5) * mm, "end": v(-15.6, -26.43) * mm});
            skArc(sketch, "E18.36.1", {"start": v(-15.6, -26.43) * mm, "mid": v(-15.73, -26.4) * mm, "end": v(-15.84, -26.45) * mm});
            skArc(sketch, "E18.36.2", {"start": v(-15.84, -26.45) * mm, "mid": v(-16.68, -27.13) * mm, "end": v(-17.6, -27.7) * mm});
            skArc(sketch, "E18.36.3", {"start": v(-17.72, -25.23) * mm, "mid": v(-17.72, -25.1) * mm, "end": v(-17.8, -25) * mm});
            skArc(sketch, "E18.36.4", {"start": v(-18.04, -24.83) * mm, "mid": v(-17.92, -24.92) * mm, "end": v(-17.8, -25) * mm});
            skArc(sketch, "E18.36.5", {"start": v(-17.72, -25.23) * mm, "mid": v(-18, -26.27) * mm, "end": v(-18.14, -27.34) * mm});
            skArc(sketch, "E18.36.6", {"start": v(-17.6, -27.7) * mm, "mid": v(-17.73, -27.6) * mm, "end": v(-17.87, -27.52) * mm});
            skArc(sketch, "E18.36.7", {"start": v(-18.14, -27.34) * mm, "mid": v(-18, -27.43) * mm, "end": v(-17.87, -27.52) * mm});
            skArc(sketch, "E18.37.0", {"start": v(-18.04, -24.83) * mm, "mid": v(-18.16, -24.74) * mm, "end": v(-18.28, -24.65) * mm});
            skArc(sketch, "E18.37.1", {"start": v(-18.28, -24.65) * mm, "mid": v(-18.4, -24.61) * mm, "end": v(-18.52, -24.65) * mm});
            skArc(sketch, "E18.37.2", {"start": v(-18.52, -24.65) * mm, "mid": v(-19.42, -25.24) * mm, "end": v(-20.4, -25.7) * mm});
            skArc(sketch, "E18.37.3", {"start": v(-20.26, -23.24) * mm, "mid": v(-20.25, -23.11) * mm, "end": v(-20.31, -23) * mm});
            skArc(sketch, "E18.37.4", {"start": v(-20.54, -22.8) * mm, "mid": v(-20.42, -22.9) * mm, "end": v(-20.31, -23) * mm});
            skArc(sketch, "E18.37.5", {"start": v(-20.26, -23.24) * mm, "mid": v(-20.65, -24.24) * mm, "end": v(-20.9, -25.3) * mm});
            skArc(sketch, "E18.37.6", {"start": v(-20.4, -25.7) * mm, "mid": v(-20.52, -25.6) * mm, "end": v(-20.65, -25.5) * mm});
            skArc(sketch, "E18.37.7", {"start": v(-20.9, -25.3) * mm, "mid": v(-20.77, -25.4) * mm, "end": v(-20.65, -25.5) * mm});
            skArc(sketch, "E18.38.0", {"start": v(-20.54, -22.8) * mm, "mid": v(-20.65, -22.7) * mm, "end": v(-20.76, -22.6) * mm});
            skArc(sketch, "E18.38.1", {"start": v(-20.76, -22.6) * mm, "mid": v(-20.87, -22.56) * mm, "end": v(-21, -22.58) * mm});
            skArc(sketch, "E18.38.2", {"start": v(-21, -22.58) * mm, "mid": v(-21.95, -23.07) * mm, "end": v(-22.97, -23.43) * mm});
            skArc(sketch, "E18.38.3", {"start": v(-22.58, -21) * mm, "mid": v(-22.56, -20.87) * mm, "end": v(-22.6, -20.76) * mm});
            skArc(sketch, "E18.38.4", {"start": v(-22.8, -20.54) * mm, "mid": v(-22.7, -20.65) * mm, "end": v(-22.6, -20.76) * mm});
            skArc(sketch, "E18.38.5", {"start": v(-22.58, -21) * mm, "mid": v(-23.07, -21.95) * mm, "end": v(-23.43, -22.97) * mm});
            skArc(sketch, "E18.38.6", {"start": v(-22.97, -23.43) * mm, "mid": v(-23.08, -23.31) * mm, "end": v(-23.2, -23.2) * mm});
            skArc(sketch, "E18.38.7", {"start": v(-23.43, -22.97) * mm, "mid": v(-23.31, -23.08) * mm, "end": v(-23.2, -23.2) * mm});
            skArc(sketch, "E18.39.0", {"start": v(-22.8, -20.54) * mm, "mid": v(-22.9, -20.42) * mm, "end": v(-23, -20.31) * mm});
            skArc(sketch, "E18.39.1", {"start": v(-23, -20.31) * mm, "mid": v(-23.11, -20.25) * mm, "end": v(-23.24, -20.26) * mm});
            skArc(sketch, "E18.39.2", {"start": v(-23.24, -20.26) * mm, "mid": v(-24.24, -20.65) * mm, "end": v(-25.3, -20.9) * mm});
            skArc(sketch, "E18.39.3", {"start": v(-24.65, -18.52) * mm, "mid": v(-24.61, -18.4) * mm, "end": v(-24.65, -18.28) * mm});
            skArc(sketch, "E18.39.4", {"start": v(-24.83, -18.04) * mm, "mid": v(-24.74, -18.16) * mm, "end": v(-24.65, -18.28) * mm});
            skArc(sketch, "E18.39.5", {"start": v(-24.65, -18.52) * mm, "mid": v(-25.24, -19.42) * mm, "end": v(-25.7, -20.4) * mm});
            skArc(sketch, "E18.39.6", {"start": v(-25.3, -20.9) * mm, "mid": v(-25.4, -20.77) * mm, "end": v(-25.5, -20.65) * mm});
            skArc(sketch, "E18.39.7", {"start": v(-25.7, -20.4) * mm, "mid": v(-25.6, -20.52) * mm, "end": v(-25.5, -20.65) * mm});
            skArc(sketch, "E18.40.0", {"start": v(-24.83, -18.04) * mm, "mid": v(-24.92, -17.92) * mm, "end": v(-25, -17.8) * mm});
            skArc(sketch, "E18.40.1", {"start": v(-25, -17.8) * mm, "mid": v(-25.1, -17.72) * mm, "end": v(-25.23, -17.72) * mm});
            skArc(sketch, "E18.40.2", {"start": v(-25.23, -17.72) * mm, "mid": v(-26.27, -18) * mm, "end": v(-27.34, -18.14) * mm});
            skArc(sketch, "E18.40.3", {"start": v(-26.45, -15.84) * mm, "mid": v(-26.4, -15.73) * mm, "end": v(-26.43, -15.6) * mm});
            skArc(sketch, "E18.40.4", {"start": v(-26.58, -15.35) * mm, "mid": v(-26.5, -15.47) * mm, "end": v(-26.43, -15.6) * mm});
            skArc(sketch, "E18.40.5", {"start": v(-26.45, -15.84) * mm, "mid": v(-27.13, -16.68) * mm, "end": v(-27.7, -17.6) * mm});
            skArc(sketch, "E18.40.6", {"start": v(-27.34, -18.14) * mm, "mid": v(-27.43, -18) * mm, "end": v(-27.52, -17.87) * mm});
            skArc(sketch, "E18.40.7", {"start": v(-27.7, -17.6) * mm, "mid": v(-27.6, -17.73) * mm, "end": v(-27.52, -17.87) * mm});
            skArc(sketch, "E18.41.0", {"start": v(-26.58, -15.35) * mm, "mid": v(-26.65, -15.22) * mm, "end": v(-26.73, -15.09) * mm});
            skArc(sketch, "E18.41.1", {"start": v(-26.73, -15.09) * mm, "mid": v(-26.82, -15) * mm, "end": v(-26.94, -15) * mm});
            skArc(sketch, "E18.41.2", {"start": v(-26.94, -15) * mm, "mid": v(-28, -15.16) * mm, "end": v(-29.08, -15.18) * mm});
            skArc(sketch, "E18.41.3", {"start": v(-27.97, -12.99) * mm, "mid": v(-27.9, -12.88) * mm, "end": v(-27.91, -12.75) * mm});
            skArc(sketch, "E18.41.4", {"start": v(-28.04, -12.48) * mm, "mid": v(-27.98, -12.62) * mm, "end": v(-27.91, -12.75) * mm});
            skArc(sketch, "E18.41.5", {"start": v(-27.97, -12.99) * mm, "mid": v(-28.73, -13.75) * mm, "end": v(-29.38, -14.6) * mm});
            skArc(sketch, "E18.41.6", {"start": v(-29.08, -15.18) * mm, "mid": v(-29.16, -15.04) * mm, "end": v(-29.23, -14.9) * mm});
            skArc(sketch, "E18.41.7", {"start": v(-29.38, -14.6) * mm, "mid": v(-29.3, -14.75) * mm, "end": v(-29.23, -14.9) * mm});
            skArc(sketch, "E18.42.0", {"start": v(-28.04, -12.48) * mm, "mid": v(-28.1, -12.35) * mm, "end": v(-28.16, -12.21) * mm});
            skArc(sketch, "E18.42.1", {"start": v(-28.16, -12.21) * mm, "mid": v(-28.24, -12.12) * mm, "end": v(-28.36, -12.1) * mm});
            skArc(sketch, "E18.42.2", {"start": v(-28.36, -12.1) * mm, "mid": v(-29.44, -12.15) * mm, "end": v(-30.51, -12.06) * mm});
            skArc(sketch, "E18.42.3", {"start": v(-29.17, -10) * mm, "mid": v(-29.1, -9.9) * mm, "end": v(-29.1, -9.77) * mm});
            skArc(sketch, "E18.42.4", {"start": v(-29.19, -9.48) * mm, "mid": v(-29.14, -9.63) * mm, "end": v(-29.1, -9.77) * mm});
            skArc(sketch, "E18.42.5", {"start": v(-29.17, -10) * mm, "mid": v(-30, -10.67) * mm, "end": v(-30.75, -11.45) * mm});
            skArc(sketch, "E18.42.6", {"start": v(-30.51, -12.06) * mm, "mid": v(-30.57, -11.9) * mm, "end": v(-30.63, -11.76) * mm});
            skArc(sketch, "E18.42.7", {"start": v(-30.75, -11.45) * mm, "mid": v(-30.69, -11.6) * mm, "end": v(-30.63, -11.76) * mm});
            skArc(sketch, "E18.43.0", {"start": v(-29.19, -9.48) * mm, "mid": v(-29.23, -9.34) * mm, "end": v(-29.28, -9.2) * mm});
            skArc(sketch, "E18.43.1", {"start": v(-29.28, -9.2) * mm, "mid": v(-29.35, -9.1) * mm, "end": v(-29.47, -9.06) * mm});
            skArc(sketch, "E18.43.2", {"start": v(-29.47, -9.06) * mm, "mid": v(-30.55, -9) * mm, "end": v(-31.6, -8.8) * mm});
            skArc(sketch, "E18.43.3", {"start": v(-30.05, -6.89) * mm, "mid": v(-29.97, -6.8) * mm, "end": v(-29.96, -6.67) * mm});
            skArc(sketch, "E18.43.4", {"start": v(-30.02, -6.38) * mm, "mid": v(-29.99, -6.53) * mm, "end": v(-29.96, -6.67) * mm});
            skArc(sketch, "E18.43.5", {"start": v(-30.05, -6.89) * mm, "mid": v(-30.96, -7.47) * mm, "end": v(-31.77, -8.18) * mm});
            skArc(sketch, "E18.43.6", {"start": v(-31.6, -8.8) * mm, "mid": v(-31.65, -8.65) * mm, "end": v(-31.7, -8.5) * mm});
            skArc(sketch, "E18.43.7", {"start": v(-31.77, -8.18) * mm, "mid": v(-31.73, -8.33) * mm, "end": v(-31.7, -8.5) * mm});
            skArc(sketch, "E18.44.0", {"start": v(-30.02, -6.38) * mm, "mid": v(-30.05, -6.24) * mm, "end": v(-30.08, -6.09) * mm});
            skArc(sketch, "E18.44.1", {"start": v(-30.08, -6.09) * mm, "mid": v(-30.14, -5.98) * mm, "end": v(-30.26, -5.93) * mm});
            skArc(sketch, "E18.44.2", {"start": v(-30.26, -5.93) * mm, "mid": v(-31.32, -5.76) * mm, "end": v(-32.35, -5.45) * mm});
            skArc(sketch, "E18.44.3", {"start": v(-30.6, -3.71) * mm, "mid": v(-30.52, -3.63) * mm, "end": v(-30.49, -3.5) * mm});
            skArc(sketch, "E18.44.4", {"start": v(-30.52, -3.2) * mm, "mid": v(-30.5, -3.36) * mm, "end": v(-30.49, -3.5) * mm});
            skArc(sketch, "E18.44.5", {"start": v(-30.6, -3.71) * mm, "mid": v(-31.57, -4.2) * mm, "end": v(-32.46, -4.81) * mm});
            skArc(sketch, "E18.44.6", {"start": v(-32.35, -5.45) * mm, "mid": v(-32.38, -5.3) * mm, "end": v(-32.4, -5.13) * mm});
            skArc(sketch, "E18.44.7", {"start": v(-32.46, -4.81) * mm, "mid": v(-32.43, -4.97) * mm, "end": v(-32.4, -5.13) * mm});
            skArc(sketch, "E18.45.0", {"start": v(-30.52, -3.2) * mm, "mid": v(-30.54, -3.06) * mm, "end": v(-30.55, -2.91) * mm});
            skArc(sketch, "E18.45.1", {"start": v(-30.55, -2.91) * mm, "mid": v(-30.6, -2.8) * mm, "end": v(-30.71, -2.73) * mm});
            skArc(sketch, "E18.45.2", {"start": v(-30.71, -2.73) * mm, "mid": v(-31.75, -2.46) * mm, "end": v(-32.75, -2.04) * mm});
            skArc(sketch, "E18.45.3", {"start": v(-30.83, -0.5) * mm, "mid": v(-30.73, -0.42) * mm, "end": v(-30.69, -0.3) * mm});
            skArc(sketch, "E18.45.4", {"start": v(-30.7, 0) * mm, "mid": v(-30.69, -0.15) * mm, "end": v(-30.69, -0.3) * mm});
            skArc(sketch, "E18.45.5", {"start": v(-30.83, -0.5) * mm, "mid": v(-31.84, -0.88) * mm, "end": v(-32.78, -1.4) * mm});
            skArc(sketch, "E18.45.6", {"start": v(-32.75, -2.04) * mm, "mid": v(-32.76, -1.88) * mm, "end": v(-32.77, -1.72) * mm});
            skArc(sketch, "E18.45.7", {"start": v(-32.78, -1.4) * mm, "mid": v(-32.77, -1.55) * mm, "end": v(-32.77, -1.72) * mm});
            skArc(sketch, "E18.46.0", {"start": v(-30.7, 0) * mm, "mid": v(-30.69, 0.15) * mm, "end": v(-30.69, 0.3) * mm});
            skArc(sketch, "E18.46.1", {"start": v(-30.69, 0.3) * mm, "mid": v(-30.73, 0.42) * mm, "end": v(-30.83, 0.5) * mm});
            skArc(sketch, "E18.46.2", {"start": v(-30.83, 0.5) * mm, "mid": v(-31.84, 0.88) * mm, "end": v(-32.78, 1.4) * mm});
            skArc(sketch, "E18.46.3", {"start": v(-30.71, 2.73) * mm, "mid": v(-30.6, 2.8) * mm, "end": v(-30.55, 2.91) * mm});
            skArc(sketch, "E18.46.4", {"start": v(-30.52, 3.2) * mm, "mid": v(-30.54, 3.06) * mm, "end": v(-30.55, 2.91) * mm});
            skArc(sketch, "E18.46.5", {"start": v(-30.71, 2.73) * mm, "mid": v(-31.75, 2.46) * mm, "end": v(-32.75, 2.04) * mm});
            skArc(sketch, "E18.46.6", {"start": v(-32.78, 1.4) * mm, "mid": v(-32.77, 1.55) * mm, "end": v(-32.77, 1.72) * mm});
            skArc(sketch, "E18.46.7", {"start": v(-32.75, 2.04) * mm, "mid": v(-32.76, 1.88) * mm, "end": v(-32.77, 1.72) * mm});
            skArc(sketch, "E18.47.0", {"start": v(-30.52, 3.2) * mm, "mid": v(-30.5, 3.36) * mm, "end": v(-30.49, 3.5) * mm});
            skArc(sketch, "E18.47.1", {"start": v(-30.49, 3.5) * mm, "mid": v(-30.52, 3.63) * mm, "end": v(-30.6, 3.71) * mm});
            skArc(sketch, "E18.47.2", {"start": v(-30.6, 3.71) * mm, "mid": v(-31.57, 4.2) * mm, "end": v(-32.46, 4.81) * mm});
            skArc(sketch, "E18.47.3", {"start": v(-30.26, 5.93) * mm, "mid": v(-30.14, 5.98) * mm, "end": v(-30.08, 6.09) * mm});
            skArc(sketch, "E18.47.4", {"start": v(-30.02, 6.38) * mm, "mid": v(-30.05, 6.24) * mm, "end": v(-30.08, 6.09) * mm});
            skArc(sketch, "E18.47.5", {"start": v(-30.26, 5.93) * mm, "mid": v(-31.32, 5.76) * mm, "end": v(-32.35, 5.45) * mm});
            skArc(sketch, "E18.47.6", {"start": v(-32.46, 4.81) * mm, "mid": v(-32.43, 4.97) * mm, "end": v(-32.4, 5.13) * mm});
            skArc(sketch, "E18.47.7", {"start": v(-32.35, 5.45) * mm, "mid": v(-32.38, 5.3) * mm, "end": v(-32.4, 5.13) * mm});
            skArc(sketch, "E18.48.0", {"start": v(-30.02, 6.38) * mm, "mid": v(-29.99, 6.53) * mm, "end": v(-29.96, 6.67) * mm});
            skArc(sketch, "E18.48.1", {"start": v(-29.96, 6.67) * mm, "mid": v(-29.97, 6.8) * mm, "end": v(-30.05, 6.89) * mm});
            skArc(sketch, "E18.48.2", {"start": v(-30.05, 6.89) * mm, "mid": v(-30.96, 7.47) * mm, "end": v(-31.77, 8.18) * mm});
            skArc(sketch, "E18.48.3", {"start": v(-29.47, 9.06) * mm, "mid": v(-29.35, 9.1) * mm, "end": v(-29.28, 9.2) * mm});
            skArc(sketch, "E18.48.4", {"start": v(-29.19, 9.48) * mm, "mid": v(-29.23, 9.34) * mm, "end": v(-29.28, 9.2) * mm});
            skArc(sketch, "E18.48.5", {"start": v(-29.47, 9.06) * mm, "mid": v(-30.55, 9) * mm, "end": v(-31.6, 8.8) * mm});
            skArc(sketch, "E18.48.6", {"start": v(-31.77, 8.18) * mm, "mid": v(-31.73, 8.33) * mm, "end": v(-31.7, 8.5) * mm});
            skArc(sketch, "E18.48.7", {"start": v(-31.6, 8.8) * mm, "mid": v(-31.65, 8.65) * mm, "end": v(-31.7, 8.5) * mm});
            skArc(sketch, "E18.49.0", {"start": v(-29.19, 9.48) * mm, "mid": v(-29.14, 9.63) * mm, "end": v(-29.1, 9.77) * mm});
            skArc(sketch, "E18.49.1", {"start": v(-29.1, 9.77) * mm, "mid": v(-29.1, 9.9) * mm, "end": v(-29.17, 10) * mm});
            skArc(sketch, "E18.49.2", {"start": v(-29.17, 10) * mm, "mid": v(-30, 10.67) * mm, "end": v(-30.75, 11.45) * mm});
            skArc(sketch, "E18.49.3", {"start": v(-28.36, 12.1) * mm, "mid": v(-28.24, 12.12) * mm, "end": v(-28.16, 12.21) * mm});
            skArc(sketch, "E18.49.4", {"start": v(-28.04, 12.48) * mm, "mid": v(-28.1, 12.35) * mm, "end": v(-28.16, 12.21) * mm});
            skArc(sketch, "E18.49.5", {"start": v(-28.36, 12.1) * mm, "mid": v(-29.44, 12.15) * mm, "end": v(-30.51, 12.06) * mm});
            skArc(sketch, "E18.49.6", {"start": v(-30.75, 11.45) * mm, "mid": v(-30.69, 11.6) * mm, "end": v(-30.63, 11.76) * mm});
            skArc(sketch, "E18.49.7", {"start": v(-30.51, 12.06) * mm, "mid": v(-30.57, 11.9) * mm, "end": v(-30.63, 11.76) * mm});
            skArc(sketch, "E18.50.0", {"start": v(-28.04, 12.48) * mm, "mid": v(-27.98, 12.62) * mm, "end": v(-27.91, 12.75) * mm});
            skArc(sketch, "E18.50.1", {"start": v(-27.91, 12.75) * mm, "mid": v(-27.9, 12.88) * mm, "end": v(-27.97, 12.99) * mm});
            skArc(sketch, "E18.50.2", {"start": v(-27.97, 12.99) * mm, "mid": v(-28.73, 13.75) * mm, "end": v(-29.38, 14.6) * mm});
            skArc(sketch, "E18.50.3", {"start": v(-26.94, 15) * mm, "mid": v(-26.82, 15) * mm, "end": v(-26.73, 15.09) * mm});
            skArc(sketch, "E18.50.4", {"start": v(-26.58, 15.35) * mm, "mid": v(-26.65, 15.22) * mm, "end": v(-26.73, 15.09) * mm});
            skArc(sketch, "E18.50.5", {"start": v(-26.94, 15) * mm, "mid": v(-28, 15.16) * mm, "end": v(-29.08, 15.18) * mm});
            skArc(sketch, "E18.50.6", {"start": v(-29.38, 14.6) * mm, "mid": v(-29.3, 14.75) * mm, "end": v(-29.23, 14.9) * mm});
            skArc(sketch, "E18.50.7", {"start": v(-29.08, 15.18) * mm, "mid": v(-29.16, 15.04) * mm, "end": v(-29.23, 14.9) * mm});
            skArc(sketch, "E18.51.0", {"start": v(-26.58, 15.34) * mm, "mid": v(-26.5, 15.47) * mm, "end": v(-26.43, 15.6) * mm});
            skArc(sketch, "E18.51.1", {"start": v(-26.43, 15.6) * mm, "mid": v(-26.4, 15.73) * mm, "end": v(-26.45, 15.84) * mm});
            skArc(sketch, "E18.51.2", {"start": v(-26.45, 15.84) * mm, "mid": v(-27.13, 16.68) * mm, "end": v(-27.7, 17.6) * mm});
            skArc(sketch, "E18.51.3", {"start": v(-25.23, 17.72) * mm, "mid": v(-25.1, 17.72) * mm, "end": v(-25, 17.8) * mm});
            skArc(sketch, "E18.51.4", {"start": v(-24.83, 18.04) * mm, "mid": v(-24.92, 17.92) * mm, "end": v(-25, 17.8) * mm});
            skArc(sketch, "E18.51.5", {"start": v(-25.23, 17.72) * mm, "mid": v(-26.27, 18) * mm, "end": v(-27.34, 18.14) * mm});
            skArc(sketch, "E18.51.6", {"start": v(-27.7, 17.6) * mm, "mid": v(-27.6, 17.73) * mm, "end": v(-27.52, 17.87) * mm});
            skArc(sketch, "E18.51.7", {"start": v(-27.34, 18.14) * mm, "mid": v(-27.43, 18) * mm, "end": v(-27.52, 17.87) * mm});
            skArc(sketch, "E18.52.0", {"start": v(-24.83, 18.04) * mm, "mid": v(-24.74, 18.16) * mm, "end": v(-24.65, 18.28) * mm});
            skArc(sketch, "E18.52.1", {"start": v(-24.65, 18.28) * mm, "mid": v(-24.61, 18.4) * mm, "end": v(-24.65, 18.52) * mm});
            skArc(sketch, "E18.52.2", {"start": v(-24.65, 18.52) * mm, "mid": v(-25.24, 19.42) * mm, "end": v(-25.7, 20.4) * mm});
            skArc(sketch, "E18.52.3", {"start": v(-23.24, 20.26) * mm, "mid": v(-23.11, 20.25) * mm, "end": v(-23, 20.31) * mm});
            skArc(sketch, "E18.52.4", {"start": v(-22.8, 20.54) * mm, "mid": v(-22.9, 20.42) * mm, "end": v(-23, 20.31) * mm});
            skArc(sketch, "E18.52.5", {"start": v(-23.24, 20.26) * mm, "mid": v(-24.24, 20.65) * mm, "end": v(-25.3, 20.9) * mm});
            skArc(sketch, "E18.52.6", {"start": v(-25.7, 20.4) * mm, "mid": v(-25.6, 20.52) * mm, "end": v(-25.5, 20.65) * mm});
            skArc(sketch, "E18.52.7", {"start": v(-25.3, 20.9) * mm, "mid": v(-25.4, 20.77) * mm, "end": v(-25.5, 20.65) * mm});
            skArc(sketch, "E18.53.0", {"start": v(-22.8, 20.54) * mm, "mid": v(-22.7, 20.65) * mm, "end": v(-22.6, 20.76) * mm});
            skArc(sketch, "E18.53.1", {"start": v(-22.6, 20.76) * mm, "mid": v(-22.56, 20.87) * mm, "end": v(-22.58, 21) * mm});
            skArc(sketch, "E18.53.2", {"start": v(-22.58, 21) * mm, "mid": v(-23.07, 21.95) * mm, "end": v(-23.43, 22.97) * mm});
            skArc(sketch, "E18.53.3", {"start": v(-21, 22.58) * mm, "mid": v(-20.87, 22.56) * mm, "end": v(-20.76, 22.6) * mm});
            skArc(sketch, "E18.53.4", {"start": v(-20.54, 22.8) * mm, "mid": v(-20.65, 22.7) * mm, "end": v(-20.76, 22.6) * mm});
            skArc(sketch, "E18.53.5", {"start": v(-21, 22.58) * mm, "mid": v(-21.95, 23.07) * mm, "end": v(-22.97, 23.43) * mm});
            skArc(sketch, "E18.53.6", {"start": v(-23.43, 22.97) * mm, "mid": v(-23.31, 23.08) * mm, "end": v(-23.2, 23.2) * mm});
            skArc(sketch, "E18.53.7", {"start": v(-22.97, 23.43) * mm, "mid": v(-23.08, 23.31) * mm, "end": v(-23.2, 23.2) * mm});
            skArc(sketch, "E18.54.0", {"start": v(-20.54, 22.8) * mm, "mid": v(-20.42, 22.9) * mm, "end": v(-20.31, 23) * mm});
            skArc(sketch, "E18.54.1", {"start": v(-20.31, 23) * mm, "mid": v(-20.25, 23.11) * mm, "end": v(-20.26, 23.24) * mm});
            skArc(sketch, "E18.54.2", {"start": v(-20.26, 23.24) * mm, "mid": v(-20.65, 24.24) * mm, "end": v(-20.9, 25.3) * mm});
            skArc(sketch, "E18.54.3", {"start": v(-18.52, 24.65) * mm, "mid": v(-18.4, 24.61) * mm, "end": v(-18.28, 24.65) * mm});
            skArc(sketch, "E18.54.4", {"start": v(-18.04, 24.83) * mm, "mid": v(-18.16, 24.74) * mm, "end": v(-18.28, 24.65) * mm});
            skArc(sketch, "E18.54.5", {"start": v(-18.52, 24.65) * mm, "mid": v(-19.42, 25.24) * mm, "end": v(-20.4, 25.7) * mm});
            skArc(sketch, "E18.54.6", {"start": v(-20.9, 25.3) * mm, "mid": v(-20.77, 25.4) * mm, "end": v(-20.65, 25.5) * mm});
            skArc(sketch, "E18.54.7", {"start": v(-20.4, 25.7) * mm, "mid": v(-20.52, 25.6) * mm, "end": v(-20.65, 25.5) * mm});
            skArc(sketch, "E18.55.0", {"start": v(-18.04, 24.83) * mm, "mid": v(-17.92, 24.92) * mm, "end": v(-17.8, 25) * mm});
            skArc(sketch, "E18.55.1", {"start": v(-17.8, 25) * mm, "mid": v(-17.72, 25.1) * mm, "end": v(-17.72, 25.23) * mm});
            skArc(sketch, "E18.55.2", {"start": v(-17.72, 25.23) * mm, "mid": v(-18, 26.27) * mm, "end": v(-18.14, 27.34) * mm});
            skArc(sketch, "E18.55.3", {"start": v(-15.84, 26.45) * mm, "mid": v(-15.73, 26.4) * mm, "end": v(-15.6, 26.43) * mm});
            skArc(sketch, "E18.55.4", {"start": v(-15.35, 26.58) * mm, "mid": v(-15.47, 26.5) * mm, "end": v(-15.6, 26.43) * mm});
            skArc(sketch, "E18.55.5", {"start": v(-15.84, 26.45) * mm, "mid": v(-16.68, 27.13) * mm, "end": v(-17.6, 27.7) * mm});
            skArc(sketch, "E18.55.6", {"start": v(-18.14, 27.34) * mm, "mid": v(-18, 27.43) * mm, "end": v(-17.87, 27.52) * mm});
            skArc(sketch, "E18.55.7", {"start": v(-17.6, 27.7) * mm, "mid": v(-17.73, 27.6) * mm, "end": v(-17.87, 27.52) * mm});
            skArc(sketch, "E18.56.0", {"start": v(-15.35, 26.58) * mm, "mid": v(-15.22, 26.65) * mm, "end": v(-15.09, 26.73) * mm});
            skArc(sketch, "E18.56.1", {"start": v(-15.09, 26.73) * mm, "mid": v(-15, 26.82) * mm, "end": v(-15, 26.94) * mm});
            skArc(sketch, "E18.56.2", {"start": v(-15, 26.94) * mm, "mid": v(-15.16, 28) * mm, "end": v(-15.18, 29.08) * mm});
            skArc(sketch, "E18.56.3", {"start": v(-12.99, 27.97) * mm, "mid": v(-12.88, 27.9) * mm, "end": v(-12.75, 27.91) * mm});
            skArc(sketch, "E18.56.4", {"start": v(-12.48, 28.04) * mm, "mid": v(-12.62, 27.98) * mm, "end": v(-12.75, 27.91) * mm});
            skArc(sketch, "E18.56.5", {"start": v(-12.99, 27.97) * mm, "mid": v(-13.75, 28.73) * mm, "end": v(-14.6, 29.38) * mm});
            skArc(sketch, "E18.56.6", {"start": v(-15.18, 29.08) * mm, "mid": v(-15.04, 29.16) * mm, "end": v(-14.9, 29.23) * mm});
            skArc(sketch, "E18.56.7", {"start": v(-14.6, 29.38) * mm, "mid": v(-14.75, 29.3) * mm, "end": v(-14.9, 29.23) * mm});
            skArc(sketch, "E18.57.0", {"start": v(-12.48, 28.04) * mm, "mid": v(-12.35, 28.1) * mm, "end": v(-12.21, 28.16) * mm});
            skArc(sketch, "E18.57.1", {"start": v(-12.21, 28.16) * mm, "mid": v(-12.12, 28.24) * mm, "end": v(-12.1, 28.36) * mm});
            skArc(sketch, "E18.57.2", {"start": v(-12.1, 28.36) * mm, "mid": v(-12.15, 29.44) * mm, "end": v(-12.06, 30.51) * mm});
            skArc(sketch, "E18.57.3", {"start": v(-10, 29.17) * mm, "mid": v(-9.9, 29.1) * mm, "end": v(-9.77, 29.1) * mm});
            skArc(sketch, "E18.57.4", {"start": v(-9.48, 29.19) * mm, "mid": v(-9.63, 29.14) * mm, "end": v(-9.77, 29.1) * mm});
            skArc(sketch, "E18.57.5", {"start": v(-10, 29.17) * mm, "mid": v(-10.67, 30) * mm, "end": v(-11.45, 30.75) * mm});
            skArc(sketch, "E18.57.6", {"start": v(-12.06, 30.51) * mm, "mid": v(-11.9, 30.57) * mm, "end": v(-11.76, 30.63) * mm});
            skArc(sketch, "E18.57.7", {"start": v(-11.45, 30.75) * mm, "mid": v(-11.6, 30.69) * mm, "end": v(-11.76, 30.63) * mm});
            skArc(sketch, "E18.58.0", {"start": v(-9.48, 29.19) * mm, "mid": v(-9.34, 29.23) * mm, "end": v(-9.2, 29.28) * mm});
            skArc(sketch, "E18.58.1", {"start": v(-9.2, 29.28) * mm, "mid": v(-9.1, 29.35) * mm, "end": v(-9.06, 29.47) * mm});
            skArc(sketch, "E18.58.2", {"start": v(-9.06, 29.47) * mm, "mid": v(-9, 30.55) * mm, "end": v(-8.8, 31.6) * mm});
            skArc(sketch, "E18.58.3", {"start": v(-6.89, 30.05) * mm, "mid": v(-6.8, 29.97) * mm, "end": v(-6.67, 29.96) * mm});
            skArc(sketch, "E18.58.4", {"start": v(-6.38, 30.02) * mm, "mid": v(-6.53, 29.99) * mm, "end": v(-6.67, 29.96) * mm});
            skArc(sketch, "E18.58.5", {"start": v(-6.89, 30.05) * mm, "mid": v(-7.47, 30.96) * mm, "end": v(-8.18, 31.77) * mm});
            skArc(sketch, "E18.58.6", {"start": v(-8.8, 31.6) * mm, "mid": v(-8.65, 31.65) * mm, "end": v(-8.5, 31.7) * mm});
            skArc(sketch, "E18.58.7", {"start": v(-8.18, 31.77) * mm, "mid": v(-8.33, 31.73) * mm, "end": v(-8.5, 31.7) * mm});
            skArc(sketch, "E18.59.0", {"start": v(-6.38, 30.02) * mm, "mid": v(-6.24, 30.05) * mm, "end": v(-6.09, 30.08) * mm});
            skArc(sketch, "E18.59.1", {"start": v(-6.09, 30.08) * mm, "mid": v(-5.98, 30.14) * mm, "end": v(-5.93, 30.26) * mm});
            skArc(sketch, "E18.59.2", {"start": v(-5.93, 30.26) * mm, "mid": v(-5.76, 31.32) * mm, "end": v(-5.45, 32.35) * mm});
            skArc(sketch, "E18.59.3", {"start": v(-3.71, 30.6) * mm, "mid": v(-3.63, 30.52) * mm, "end": v(-3.5, 30.49) * mm});
            skArc(sketch, "E18.59.4", {"start": v(-3.2, 30.52) * mm, "mid": v(-3.36, 30.5) * mm, "end": v(-3.5, 30.49) * mm});
            skArc(sketch, "E18.59.5", {"start": v(-3.71, 30.6) * mm, "mid": v(-4.2, 31.57) * mm, "end": v(-4.81, 32.46) * mm});
            skArc(sketch, "E18.59.6", {"start": v(-5.45, 32.35) * mm, "mid": v(-5.3, 32.38) * mm, "end": v(-5.13, 32.4) * mm});
            skArc(sketch, "E18.59.7", {"start": v(-4.81, 32.46) * mm, "mid": v(-4.97, 32.43) * mm, "end": v(-5.13, 32.4) * mm});
            skLineSegment(sketch, "E18.anchor1", {"start": v(0, 0) * mm, "end": v(-8.08, 28.5) * mm, "construction": true});
            skLineSegment(sketch, "E18.anchor2", {"start": v(0, 0) * mm, "end": v(-11.02, 27.5) * mm, "construction": true});
            skSolve(sketch);
        }
        {
            var Q0;
            Q0=makeQuery(id+"F0.imprint","IMPRINT",FACE,{"disambiguationData":[TD([[makeQuery(id+"F0.imprint","IMPRINT",EDGE,{"derivedFrom":sQuery(id+"F0.wireOp",EDGE,"E10")}),1.0]])]});
            extrude(context, id + "F1", {"entities" : qUnion([Q0]), "depth" : 5 * mm, "offsetDistance" : 25 * mm});
        }
        {
            var Q0;
            Q0=qCreatedBy(makeId("Front.planeOp"),FACE);
            var sketch = newSketch(context, id + "F2", { "sketchPlane" : qUnion([Q0])});
            skArc(sketch, "E19.0.263", {"start": v(1.4, 32.78) * mm, "mid": v(0.88, 31.84) * mm, "end": v(0.5, 30.83) * mm});
            skArc(sketch, "E19.0.264", {"start": v(0.5, 30.83) * mm, "mid": v(0.42, 30.73) * mm, "end": v(0.3, 30.69) * mm});
            skArc(sketch, "E19.0.265", {"start": v(0.3, 30.69) * mm, "mid": v(0, 30.7) * mm, "end": v(-0.3, 30.69) * mm});
            skArc(sketch, "E19.0.266", {"start": v(-0.3, 30.69) * mm, "mid": v(-0.42, 30.73) * mm, "end": v(-0.5, 30.83) * mm});
            skArc(sketch, "E19.0.267", {"start": v(-0.5, 30.83) * mm, "mid": v(-0.88, 31.84) * mm, "end": v(-1.4, 32.78) * mm});
            skLineSegment(sketch, "E20", {"start": v(0, 29.1) * mm, "end": v(0, 33.7) * mm, "construction": true});
            skLineSegment(sketch, "E21", {"start": v(1.18, 33.1) * mm, "end": v(0.48, 31.15) * mm});
            skLineSegment(sketch, "E22", {"start": v(0.1, 30.89) * mm, "end": v(0, 30.89) * mm});
            skPoint(sketch, "E23.orphan", {"position": v(-0.2, 30.38) * mm});
            skPoint(sketch, "E24.orphan", {"position": v(0.2, 30.38) * mm});
            skPoint(sketch, "E25.visualSharp", {"position": v(0.38, 30.89) * mm});
            skArc(sketch, "E25.filletArc", {"start": v(0.1, 30.89) * mm, "mid": v(0.33, 30.96) * mm, "end": v(0.48, 31.15) * mm});
            skPoint(sketch, "E26.orphan", {"position": v(-0.4, 30.89) * mm});
            skLineSegment(sketch, "E27.MirrorCS", {"start": v(-0.1, 30.89) * mm, "end": v(0, 30.89) * mm});
            skArc(sketch, "E28.MirrorCS", {"start": v(-0.1, 30.89) * mm, "mid": v(-0.33, 30.96) * mm, "end": v(-0.48, 31.15) * mm});
            skLineSegment(sketch, "E29.MirrorCS", {"start": v(-1.18, 33.1) * mm, "end": v(-0.48, 31.15) * mm});
            skLineSegment(sketch, "E30.1.0.0", {"start": v(4.5, 33.1) * mm, "end": v(3.8, 31.15) * mm});
            skArc(sketch, "E30.1.0.1", {"start": v(3.42, 30.89) * mm, "mid": v(3.65, 30.96) * mm, "end": v(3.8, 31.15) * mm});
            skLineSegment(sketch, "E30.1.0.2", {"start": v(3.42, 30.89) * mm, "end": v(3.32, 30.89) * mm});
            skLineSegment(sketch, "E30.1.0.3", {"start": v(3.22, 30.89) * mm, "end": v(3.32, 30.89) * mm});
            skArc(sketch, "E30.1.0.4", {"start": v(3.22, 30.89) * mm, "mid": v(3, 30.96) * mm, "end": v(2.85, 31.15) * mm});
            skLineSegment(sketch, "E30.1.0.5", {"start": v(2.14, 33.1) * mm, "end": v(2.85, 31.15) * mm});
            skLineSegment(sketch, "E30.2.0.0", {"start": v(7.83, 33.1) * mm, "end": v(7.13, 31.15) * mm});
            skArc(sketch, "E30.2.0.1", {"start": v(6.75, 30.89) * mm, "mid": v(6.98, 30.96) * mm, "end": v(7.13, 31.15) * mm});
            skLineSegment(sketch, "E30.2.0.2", {"start": v(6.75, 30.89) * mm, "end": v(6.65, 30.89) * mm});
            skLineSegment(sketch, "E30.2.0.3", {"start": v(6.55, 30.89) * mm, "end": v(6.65, 30.89) * mm});
            skArc(sketch, "E30.2.0.4", {"start": v(6.55, 30.89) * mm, "mid": v(6.32, 30.96) * mm, "end": v(6.17, 31.15) * mm});
            skLineSegment(sketch, "E30.2.0.5", {"start": v(5.47, 33.1) * mm, "end": v(6.17, 31.15) * mm});
            skLineSegment(sketch, "E30.3.0.0", {"start": v(11.16, 33.1) * mm, "end": v(10.45, 31.15) * mm});
            skArc(sketch, "E30.3.0.1", {"start": v(10.07, 30.89) * mm, "mid": v(10.3, 30.96) * mm, "end": v(10.45, 31.15) * mm});
            skLineSegment(sketch, "E30.3.0.2", {"start": v(10.07, 30.89) * mm, "end": v(9.97, 30.89) * mm});
            skLineSegment(sketch, "E30.3.0.3", {"start": v(9.87, 30.89) * mm, "end": v(9.97, 30.89) * mm});
            skArc(sketch, "E30.3.0.4", {"start": v(9.87, 30.89) * mm, "mid": v(9.64, 30.96) * mm, "end": v(9.5, 31.15) * mm});
            skLineSegment(sketch, "E30.3.0.5", {"start": v(8.8, 33.1) * mm, "end": v(9.5, 31.15) * mm});
            skLineSegment(sketch, "E30.4.0.0", {"start": v(14.48, 33.1) * mm, "end": v(13.78, 31.15) * mm});
            skArc(sketch, "E30.4.0.1", {"start": v(13.4, 30.89) * mm, "mid": v(13.63, 30.96) * mm, "end": v(13.78, 31.15) * mm});
            skLineSegment(sketch, "E30.4.0.2", {"start": v(13.4, 30.89) * mm, "end": v(13.3, 30.89) * mm});
            skLineSegment(sketch, "E30.4.0.3", {"start": v(13.2, 30.89) * mm, "end": v(13.3, 30.89) * mm});
            skArc(sketch, "E30.4.0.4", {"start": v(13.2, 30.89) * mm, "mid": v(12.97, 30.96) * mm, "end": v(12.82, 31.15) * mm});
            skLineSegment(sketch, "E30.4.0.5", {"start": v(12.12, 33.1) * mm, "end": v(12.82, 31.15) * mm});
            skLineSegment(sketch, "E30.5.0.0", {"start": v(17.8, 33.1) * mm, "end": v(17.1, 31.15) * mm});
            skArc(sketch, "E30.5.0.1", {"start": v(16.72, 30.89) * mm, "mid": v(16.95, 30.96) * mm, "end": v(17.1, 31.15) * mm});
            skLineSegment(sketch, "E30.5.0.2", {"start": v(16.72, 30.89) * mm, "end": v(16.62, 30.89) * mm});
            skLineSegment(sketch, "E30.5.0.3", {"start": v(16.52, 30.89) * mm, "end": v(16.62, 30.89) * mm});
            skArc(sketch, "E30.5.0.4", {"start": v(16.52, 30.89) * mm, "mid": v(16.3, 30.96) * mm, "end": v(16.15, 31.15) * mm});
            skLineSegment(sketch, "E30.5.0.5", {"start": v(15.44, 33.1) * mm, "end": v(16.15, 31.15) * mm});
            skLineSegment(sketch, "E30.6.0.0", {"start": v(21.13, 33.1) * mm, "end": v(20.42, 31.15) * mm});
            skArc(sketch, "E30.6.0.1", {"start": v(20.05, 30.89) * mm, "mid": v(20.28, 30.96) * mm, "end": v(20.42, 31.15) * mm});
            skLineSegment(sketch, "E30.6.0.2", {"start": v(20.05, 30.89) * mm, "end": v(19.95, 30.89) * mm});
            skLineSegment(sketch, "E30.6.0.3", {"start": v(19.85, 30.89) * mm, "end": v(19.95, 30.89) * mm});
            skArc(sketch, "E30.6.0.4", {"start": v(19.85, 30.89) * mm, "mid": v(19.62, 30.96) * mm, "end": v(19.47, 31.15) * mm});
            skLineSegment(sketch, "E30.6.0.5", {"start": v(18.77, 33.1) * mm, "end": v(19.47, 31.15) * mm});
            skLineSegment(sketch, "E30.7.0.0", {"start": v(24.45, 33.1) * mm, "end": v(23.75, 31.15) * mm});
            skArc(sketch, "E30.7.0.1", {"start": v(23.37, 30.89) * mm, "mid": v(23.6, 30.96) * mm, "end": v(23.75, 31.15) * mm});
            skLineSegment(sketch, "E30.7.0.2", {"start": v(23.37, 30.89) * mm, "end": v(23.27, 30.89) * mm});
            skLineSegment(sketch, "E30.7.0.3", {"start": v(23.17, 30.89) * mm, "end": v(23.27, 30.89) * mm});
            skArc(sketch, "E30.7.0.4", {"start": v(23.17, 30.89) * mm, "mid": v(22.94, 30.96) * mm, "end": v(22.8, 31.15) * mm});
            skLineSegment(sketch, "E30.7.0.5", {"start": v(22.1, 33.1) * mm, "end": v(22.8, 31.15) * mm});
            skLineSegment(sketch, "E30.direction1", {"start": v(-0.48, 31.15) * mm, "end": v(2.85, 31.15) * mm, "construction": true});
            skLineSegment(sketch, "E31", {"start": v(1.18, 33.1) * mm, "end": v(2.14, 33.1) * mm});
            skLineSegment(sketch, "E32", {"start": v(4.5, 33.1) * mm, "end": v(5.47, 33.1) * mm});
            skLineSegment(sketch, "E33", {"start": v(7.83, 33.1) * mm, "end": v(8.8, 33.1) * mm});
            skLineSegment(sketch, "E34", {"start": v(11.16, 33.1) * mm, "end": v(12.12, 33.1) * mm});
            skLineSegment(sketch, "E35", {"start": v(14.48, 33.1) * mm, "end": v(15.44, 33.1) * mm});
            skLineSegment(sketch, "E36", {"start": v(17.8, 33.1) * mm, "end": v(18.77, 33.1) * mm});
            skLineSegment(sketch, "E37", {"start": v(21.13, 33.1) * mm, "end": v(22.1, 33.1) * mm});
            skLineSegment(sketch, "E38.1.0.0", {"start": v(-2.14, 33.1) * mm, "end": v(-2.85, 31.15) * mm});
            skArc(sketch, "E38.1.0.1", {"start": v(-3.23, 30.89) * mm, "mid": v(-3, 30.96) * mm, "end": v(-2.85, 31.15) * mm});
            skLineSegment(sketch, "E38.1.0.2", {"start": v(-3.23, 30.89) * mm, "end": v(-3.33, 30.89) * mm});
            skLineSegment(sketch, "E38.1.0.3", {"start": v(-3.43, 30.89) * mm, "end": v(-3.33, 30.89) * mm});
            skArc(sketch, "E38.1.0.4", {"start": v(-3.43, 30.89) * mm, "mid": v(-3.65, 30.96) * mm, "end": v(-3.8, 31.15) * mm});
            skLineSegment(sketch, "E38.1.0.5", {"start": v(-4.5, 33.1) * mm, "end": v(-3.8, 31.15) * mm});
            skLineSegment(sketch, "E38.2.0.0", {"start": v(-5.47, 33.1) * mm, "end": v(-6.17, 31.15) * mm});
            skArc(sketch, "E38.2.0.1", {"start": v(-6.55, 30.89) * mm, "mid": v(-6.32, 30.96) * mm, "end": v(-6.17, 31.15) * mm});
            skLineSegment(sketch, "E38.2.0.2", {"start": v(-6.55, 30.89) * mm, "end": v(-6.65, 30.89) * mm});
            skLineSegment(sketch, "E38.2.0.3", {"start": v(-6.75, 30.89) * mm, "end": v(-6.65, 30.89) * mm});
            skArc(sketch, "E38.2.0.4", {"start": v(-6.75, 30.89) * mm, "mid": v(-6.98, 30.96) * mm, "end": v(-7.13, 31.15) * mm});
            skLineSegment(sketch, "E38.2.0.5", {"start": v(-7.83, 33.1) * mm, "end": v(-7.13, 31.15) * mm});
            skLineSegment(sketch, "E38.3.0.0", {"start": v(-8.8, 33.1) * mm, "end": v(-9.5, 31.15) * mm});
            skArc(sketch, "E38.3.0.1", {"start": v(-9.88, 30.89) * mm, "mid": v(-9.65, 30.96) * mm, "end": v(-9.5, 31.15) * mm});
            skLineSegment(sketch, "E38.3.0.2", {"start": v(-9.88, 30.89) * mm, "end": v(-9.98, 30.89) * mm});
            skLineSegment(sketch, "E38.3.0.3", {"start": v(-10.08, 30.89) * mm, "end": v(-9.98, 30.89) * mm});
            skArc(sketch, "E38.3.0.4", {"start": v(-10.08, 30.89) * mm, "mid": v(-10.3, 30.96) * mm, "end": v(-10.45, 31.15) * mm});
            skLineSegment(sketch, "E38.3.0.5", {"start": v(-11.16, 33.1) * mm, "end": v(-10.45, 31.15) * mm});
            skLineSegment(sketch, "E38.4.0.0", {"start": v(-12.12, 33.1) * mm, "end": v(-12.82, 31.15) * mm});
            skArc(sketch, "E38.4.0.1", {"start": v(-13.2, 30.89) * mm, "mid": v(-12.97, 30.96) * mm, "end": v(-12.82, 31.15) * mm});
            skLineSegment(sketch, "E38.4.0.2", {"start": v(-13.2, 30.89) * mm, "end": v(-13.3, 30.89) * mm});
            skLineSegment(sketch, "E38.4.0.3", {"start": v(-13.4, 30.89) * mm, "end": v(-13.3, 30.89) * mm});
            skArc(sketch, "E38.4.0.4", {"start": v(-13.4, 30.89) * mm, "mid": v(-13.63, 30.96) * mm, "end": v(-13.78, 31.15) * mm});
            skLineSegment(sketch, "E38.4.0.5", {"start": v(-14.48, 33.1) * mm, "end": v(-13.78, 31.15) * mm});
            skLineSegment(sketch, "E38.5.0.0", {"start": v(-15.44, 33.1) * mm, "end": v(-16.15, 31.15) * mm});
            skArc(sketch, "E38.5.0.1", {"start": v(-16.53, 30.89) * mm, "mid": v(-16.3, 30.96) * mm, "end": v(-16.15, 31.15) * mm});
            skLineSegment(sketch, "E38.5.0.2", {"start": v(-16.53, 30.89) * mm, "end": v(-16.62, 30.89) * mm});
            skLineSegment(sketch, "E38.5.0.3", {"start": v(-16.73, 30.89) * mm, "end": v(-16.62, 30.89) * mm});
            skArc(sketch, "E38.5.0.4", {"start": v(-16.73, 30.89) * mm, "mid": v(-16.95, 30.96) * mm, "end": v(-17.1, 31.15) * mm});
            skLineSegment(sketch, "E38.5.0.5", {"start": v(-17.8, 33.1) * mm, "end": v(-17.1, 31.15) * mm});
            skLineSegment(sketch, "E38.6.0.0", {"start": v(-18.77, 33.1) * mm, "end": v(-19.47, 31.15) * mm});
            skArc(sketch, "E38.6.0.1", {"start": v(-19.85, 30.89) * mm, "mid": v(-19.62, 30.96) * mm, "end": v(-19.47, 31.15) * mm});
            skLineSegment(sketch, "E38.6.0.2", {"start": v(-19.85, 30.89) * mm, "end": v(-19.95, 30.89) * mm});
            skLineSegment(sketch, "E38.6.0.3", {"start": v(-20.05, 30.89) * mm, "end": v(-19.95, 30.89) * mm});
            skArc(sketch, "E38.6.0.4", {"start": v(-20.05, 30.89) * mm, "mid": v(-20.28, 30.96) * mm, "end": v(-20.43, 31.15) * mm});
            skLineSegment(sketch, "E38.6.0.5", {"start": v(-21.13, 33.1) * mm, "end": v(-20.43, 31.15) * mm});
            skLineSegment(sketch, "E38.7.0.0", {"start": v(-22.1, 33.1) * mm, "end": v(-22.8, 31.15) * mm});
            skArc(sketch, "E38.7.0.1", {"start": v(-23.18, 30.89) * mm, "mid": v(-22.95, 30.96) * mm, "end": v(-22.8, 31.15) * mm});
            skLineSegment(sketch, "E38.7.0.2", {"start": v(-23.18, 30.89) * mm, "end": v(-23.28, 30.89) * mm});
            skLineSegment(sketch, "E38.7.0.3", {"start": v(-23.38, 30.89) * mm, "end": v(-23.28, 30.89) * mm});
            skArc(sketch, "E38.7.0.4", {"start": v(-23.38, 30.89) * mm, "mid": v(-23.6, 30.96) * mm, "end": v(-23.75, 31.15) * mm});
            skLineSegment(sketch, "E38.7.0.5", {"start": v(-24.46, 33.1) * mm, "end": v(-23.75, 31.15) * mm});
            skLineSegment(sketch, "E38.direction1", {"start": v(-0.48, 31.15) * mm, "end": v(-3.8, 31.15) * mm, "construction": true});
            skLineSegment(sketch, "E39", {"start": v(-1.18, 33.1) * mm, "end": v(-2.14, 33.1) * mm});
            skLineSegment(sketch, "E40", {"start": v(-4.5, 33.1) * mm, "end": v(-5.47, 33.1) * mm});
            skLineSegment(sketch, "E41", {"start": v(-7.83, 33.1) * mm, "end": v(-8.8, 33.1) * mm});
            skLineSegment(sketch, "E42", {"start": v(-11.16, 33.1) * mm, "end": v(-12.12, 33.1) * mm});
            skLineSegment(sketch, "E43", {"start": v(-14.48, 33.1) * mm, "end": v(-15.44, 33.1) * mm});
            skLineSegment(sketch, "E44", {"start": v(-17.8, 33.1) * mm, "end": v(-18.77, 33.1) * mm});
            skLineSegment(sketch, "E45", {"start": v(-21.13, 33.1) * mm, "end": v(-22.1, 33.1) * mm});
            skLineSegment(sketch, "E46.top", {"start": v(27.54, 43.1) * mm, "end": v(-27.46, 43.1) * mm});
            skLineSegment(sketch, "E46.left", {"start": v(27.54, 33.1) * mm, "end": v(27.54, 43.1) * mm});
            skLineSegment(sketch, "E46.right", {"start": v(-27.46, 33.1) * mm, "end": v(-27.46, 43.1) * mm});
            skLineSegment(sketch, "E47", {"start": v(24.45, 33.1) * mm, "end": v(27.54, 33.1) * mm});
            skLineSegment(sketch, "E48", {"start": v(-24.46, 33.1) * mm, "end": v(-27.46, 33.1) * mm});
            skSolve(sketch);
        }
        {
            var Q0;
            Q0 = qSketchRegion(id + "F2", true);
            extrude(context, id + "F3", {"entities" : qUnion([Q0]), "depth" : 5 * mm, "offsetDistance" : 25 * mm});
        }
    });
